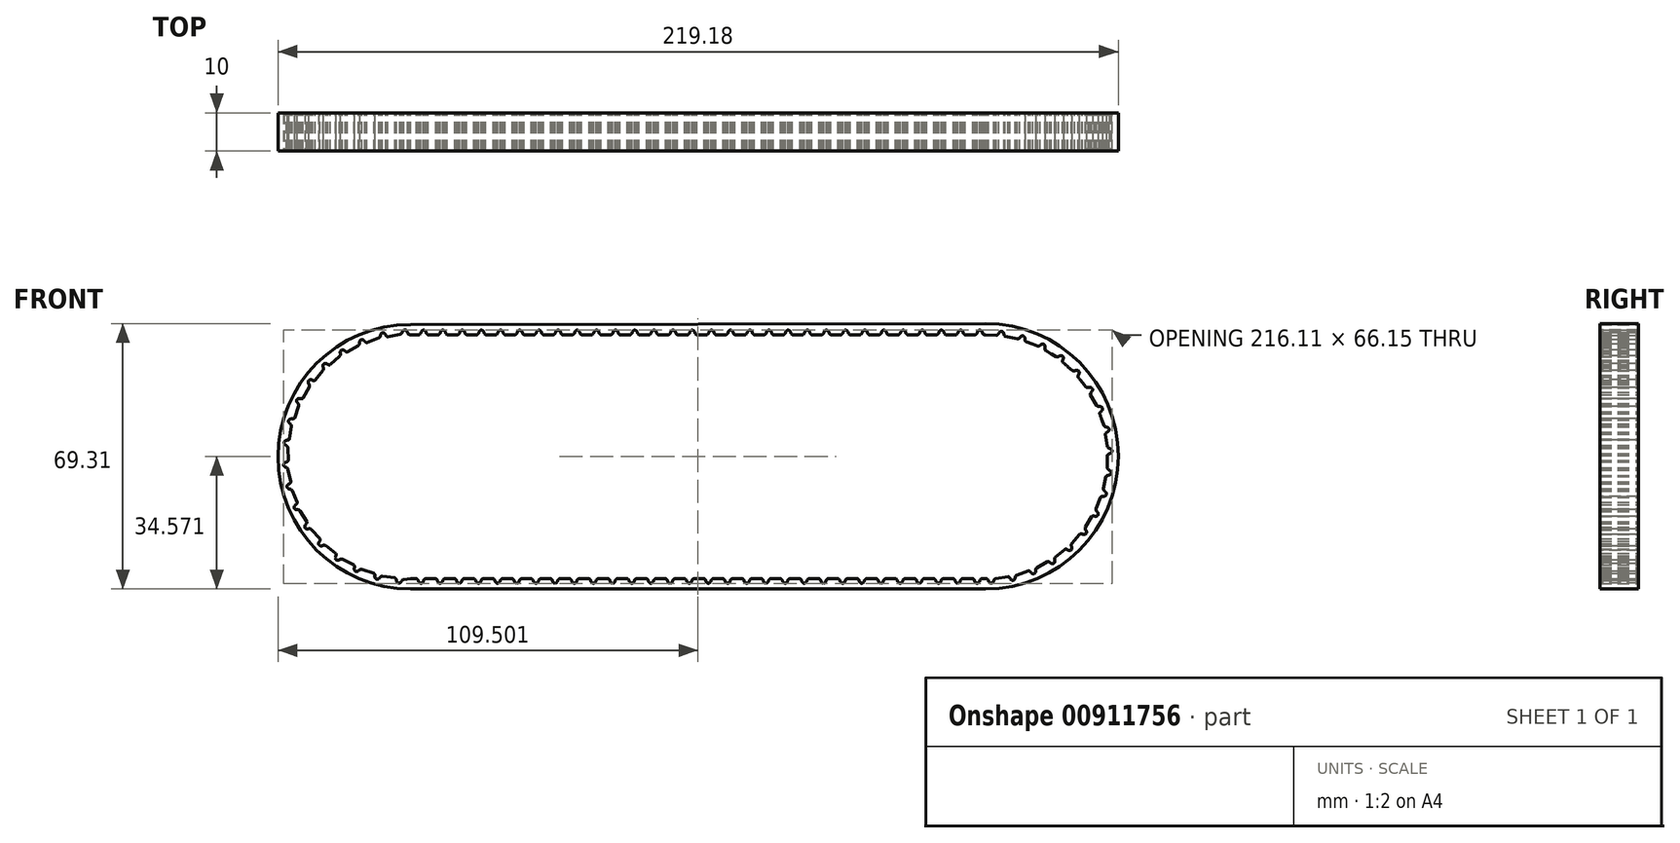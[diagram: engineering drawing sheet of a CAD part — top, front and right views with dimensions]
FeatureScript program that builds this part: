
annotation { "Feature Type Name" : "Feature", "Feature Type Description" : "" }
export const myFeature = defineFeature(function(context is Context, id is Id, definition is map)
    precondition{}
    {
        {
            var Q0;
            Q0=qCreatedBy(makeId("Front.planeOp"),FACE);
            var sketch = newSketch(context, id + "F0", { "sketchPlane" : qUnion([Q0])});
            skLineSegment(sketch, "E0", {"start": v(-83.51, -31.83) * mm, "end": v(-83.51, -31.83) * mm});
            skLineSegment(sketch, "E1", {"start": v(66.49, 31.83) * mm, "end": v(66.49, 31.83) * mm});
            skLineSegment(sketch, "E2", {"start": v(-83.51, 31.83) * mm, "end": v(-81.28, 31.83) * mm});
            skLineSegment(sketch, "E3", {"start": v(-83.51, -31.83) * mm, "end": v(-82.23, -31.83) * mm});
            skLineSegment(sketch, "E4", {"start": v(-83.51, -34.53) * mm, "end": v(-83.51, -34.53) * mm});
            skArc(sketch, "E5", {"start": v(66.49, 34.78) * mm, "mid": v(66.46, 34.78) * mm, "end": v(66.43, 34.78) * mm});
            skLineSegment(sketch, "E6", {"start": v(-83.51, -34.53) * mm, "end": v(66.49, -34.53) * mm});
            skArc(sketch, "E7", {"start": v(-83.51, 31.83) * mm, "mid": v(-83.53, 31.83) * mm, "end": v(-83.54, 31.83) * mm});
            skPoint(sketch, "E8", {"position": v(-75, 33.03) * mm});
            skEllipticalArc(sketch, "E9.1.0.0", {});
            skPoint(sketch, "E9.1.0.1", {"position": v(-70, 33.03) * mm});
            skArc(sketch, "E9.1.0.2", {"start": v(-69.27, 32.27) * mm, "mid": v(-69.1, 32) * mm, "end": v(-68.85, 31.83) * mm});
            skEllipticalArc(sketch, "E9.2.0.0", {});
            skPoint(sketch, "E9.2.0.1", {"position": v(-65, 33.03) * mm});
            skArc(sketch, "E9.2.0.2", {"start": v(-64.27, 32.27) * mm, "mid": v(-64.1, 32) * mm, "end": v(-63.85, 31.83) * mm});
            skEllipticalArc(sketch, "E9.3.0.0", {});
            skPoint(sketch, "E9.3.0.1", {"position": v(-60, 33.03) * mm});
            skArc(sketch, "E9.3.0.2", {"start": v(-59.27, 32.27) * mm, "mid": v(-59.1, 32) * mm, "end": v(-58.85, 31.83) * mm});
            skEllipticalArc(sketch, "E9.4.0.0", {});
            skPoint(sketch, "E9.4.0.1", {"position": v(-55, 33.03) * mm});
            skArc(sketch, "E9.4.0.2", {"start": v(-54.27, 32.27) * mm, "mid": v(-54.1, 32) * mm, "end": v(-53.85, 31.83) * mm});
            skEllipticalArc(sketch, "E9.5.0.0", {});
            skPoint(sketch, "E9.5.0.1", {"position": v(-50, 33.03) * mm});
            skArc(sketch, "E9.5.0.2", {"start": v(-49.27, 32.27) * mm, "mid": v(-49.1, 32) * mm, "end": v(-48.85, 31.83) * mm});
            skEllipticalArc(sketch, "E9.6.0.0", {});
            skPoint(sketch, "E9.6.0.1", {"position": v(-45, 33.03) * mm});
            skArc(sketch, "E9.6.0.2", {"start": v(-44.27, 32.27) * mm, "mid": v(-44.1, 32) * mm, "end": v(-43.85, 31.83) * mm});
            skEllipticalArc(sketch, "E9.7.0.0", {});
            skPoint(sketch, "E9.7.0.1", {"position": v(-40, 33.03) * mm});
            skArc(sketch, "E9.7.0.2", {"start": v(-39.27, 32.27) * mm, "mid": v(-39.1, 32) * mm, "end": v(-38.85, 31.83) * mm});
            skEllipticalArc(sketch, "E9.8.0.0", {});
            skPoint(sketch, "E9.8.0.1", {"position": v(-35, 33.03) * mm});
            skArc(sketch, "E9.8.0.2", {"start": v(-34.27, 32.27) * mm, "mid": v(-34.1, 32) * mm, "end": v(-33.85, 31.83) * mm});
            skEllipticalArc(sketch, "E9.9.0.0", {});
            skPoint(sketch, "E9.9.0.1", {"position": v(-30, 33.03) * mm});
            skArc(sketch, "E9.9.0.2", {"start": v(-29.27, 32.27) * mm, "mid": v(-29.1, 32) * mm, "end": v(-28.85, 31.83) * mm});
            skEllipticalArc(sketch, "E9.10.0.0", {});
            skPoint(sketch, "E9.10.0.1", {"position": v(-25, 33.03) * mm});
            skArc(sketch, "E9.10.0.2", {"start": v(-24.27, 32.27) * mm, "mid": v(-24.1, 32) * mm, "end": v(-23.85, 31.83) * mm});
            skEllipticalArc(sketch, "E9.11.0.0", {});
            skPoint(sketch, "E9.11.0.1", {"position": v(-20, 33.03) * mm});
            skArc(sketch, "E9.11.0.2", {"start": v(-19.27, 32.27) * mm, "mid": v(-19.1, 32) * mm, "end": v(-18.85, 31.83) * mm});
            skEllipticalArc(sketch, "E9.12.0.0", {});
            skPoint(sketch, "E9.12.0.1", {"position": v(-15, 33.03) * mm});
            skArc(sketch, "E9.12.0.2", {"start": v(-14.27, 32.27) * mm, "mid": v(-14.1, 32) * mm, "end": v(-13.85, 31.83) * mm});
            skEllipticalArc(sketch, "E9.13.0.0", {});
            skPoint(sketch, "E9.13.0.1", {"position": v(-10, 33.03) * mm});
            skArc(sketch, "E9.13.0.2", {"start": v(-9.27, 32.27) * mm, "mid": v(-9.1, 32) * mm, "end": v(-8.85, 31.83) * mm});
            skEllipticalArc(sketch, "E9.14.0.0", {});
            skPoint(sketch, "E9.14.0.1", {"position": v(-5, 33.03) * mm});
            skArc(sketch, "E9.14.0.2", {"start": v(-4.27, 32.27) * mm, "mid": v(-4.1, 32) * mm, "end": v(-3.85, 31.83) * mm});
            skEllipticalArc(sketch, "E9.15.0.0", {});
            skPoint(sketch, "E9.15.0.1", {"position": v(0, 33.03) * mm});
            skArc(sketch, "E9.15.0.2", {"start": v(0.73, 32.27) * mm, "mid": v(0.9, 32) * mm, "end": v(1.15, 31.83) * mm});
            skEllipticalArc(sketch, "E9.16.0.0", {});
            skPoint(sketch, "E9.16.0.1", {"position": v(5, 33.03) * mm});
            skArc(sketch, "E9.16.0.2", {"start": v(5.73, 32.27) * mm, "mid": v(5.9, 32) * mm, "end": v(6.15, 31.83) * mm});
            skEllipticalArc(sketch, "E9.17.0.0", {});
            skPoint(sketch, "E9.17.0.1", {"position": v(10, 33.03) * mm});
            skArc(sketch, "E9.17.0.2", {"start": v(10.73, 32.27) * mm, "mid": v(10.9, 32) * mm, "end": v(11.15, 31.83) * mm});
            skEllipticalArc(sketch, "E9.18.0.0", {});
            skPoint(sketch, "E9.18.0.1", {"position": v(15, 33.03) * mm});
            skArc(sketch, "E9.18.0.2", {"start": v(15.73, 32.27) * mm, "mid": v(15.9, 32) * mm, "end": v(16.15, 31.83) * mm});
            skEllipticalArc(sketch, "E9.19.0.0", {});
            skPoint(sketch, "E9.19.0.1", {"position": v(20, 33.03) * mm});
            skArc(sketch, "E9.19.0.2", {"start": v(20.73, 32.27) * mm, "mid": v(20.9, 32) * mm, "end": v(21.15, 31.83) * mm});
            skEllipticalArc(sketch, "E9.20.0.0", {});
            skPoint(sketch, "E9.20.0.1", {"position": v(25, 33.03) * mm});
            skArc(sketch, "E9.20.0.2", {"start": v(25.73, 32.27) * mm, "mid": v(25.9, 32) * mm, "end": v(26.15, 31.83) * mm});
            skEllipticalArc(sketch, "E9.21.0.0", {});
            skPoint(sketch, "E9.21.0.1", {"position": v(30, 33.03) * mm});
            skArc(sketch, "E9.21.0.2", {"start": v(30.73, 32.27) * mm, "mid": v(30.9, 32) * mm, "end": v(31.15, 31.83) * mm});
            skEllipticalArc(sketch, "E9.22.0.0", {});
            skPoint(sketch, "E9.22.0.1", {"position": v(35, 33.03) * mm});
            skArc(sketch, "E9.22.0.2", {"start": v(35.73, 32.27) * mm, "mid": v(35.9, 32) * mm, "end": v(36.15, 31.83) * mm});
            skEllipticalArc(sketch, "E9.23.0.0", {});
            skPoint(sketch, "E9.23.0.1", {"position": v(40, 33.03) * mm});
            skArc(sketch, "E9.23.0.2", {"start": v(40.73, 32.27) * mm, "mid": v(40.9, 32) * mm, "end": v(41.15, 31.83) * mm});
            skEllipticalArc(sketch, "E9.24.0.0", {});
            skPoint(sketch, "E9.24.0.1", {"position": v(45, 33.03) * mm});
            skArc(sketch, "E9.24.0.2", {"start": v(45.73, 32.27) * mm, "mid": v(45.9, 32) * mm, "end": v(46.15, 31.83) * mm});
            skEllipticalArc(sketch, "E9.25.0.0", {});
            skPoint(sketch, "E9.25.0.1", {"position": v(50, 33.03) * mm});
            skArc(sketch, "E9.25.0.2", {"start": v(50.73, 32.27) * mm, "mid": v(50.9, 32) * mm, "end": v(51.15, 31.83) * mm});
            skEllipticalArc(sketch, "E9.26.0.0", {});
            skPoint(sketch, "E9.26.0.1", {"position": v(55, 33.03) * mm});
            skArc(sketch, "E9.26.0.2", {"start": v(55.73, 32.27) * mm, "mid": v(55.9, 32) * mm, "end": v(56.15, 31.83) * mm});
            skEllipticalArc(sketch, "E9.27.0.0", {});
            skPoint(sketch, "E9.27.0.1", {"position": v(60, 33.03) * mm});
            skArc(sketch, "E9.27.0.2", {"start": v(60.73, 32.27) * mm, "mid": v(60.9, 32) * mm, "end": v(61.15, 31.83) * mm});
            skEllipticalArc(sketch, "E9.28.0.0", {});
            skPoint(sketch, "E9.28.0.1", {"position": v(65, 33.03) * mm});
            skArc(sketch, "E9.28.0.2", {"start": v(65.73, 32.27) * mm, "mid": v(65.9, 32) * mm, "end": v(66.15, 31.83) * mm});
            skLineSegment(sketch, "E9.direction1", {"start": v(-75, 32.03) * mm, "end": v(-70, 32.03) * mm, "construction": true});
            skEllipticalArc(sketch, "E10", {});
            skArc(sketch, "E11", {"start": v(-71.2, 31.83) * mm, "mid": v(-70.9, 32) * mm, "end": v(-70.7, 32.27) * mm});
            skEllipticalArc(sketch, "E12.1.0.0", {});
            skArc(sketch, "E12.1.0.1", {"start": v(-66.2, 31.83) * mm, "mid": v(-65.9, 32) * mm, "end": v(-65.7, 32.27) * mm});
            skEllipticalArc(sketch, "E12.2.0.0", {});
            skArc(sketch, "E12.2.0.1", {"start": v(-61.2, 31.83) * mm, "mid": v(-60.9, 32) * mm, "end": v(-60.7, 32.27) * mm});
            skEllipticalArc(sketch, "E13.0.3.0", {});
            skArc(sketch, "E13.4.3.0", {"start": v(-56.2, 31.83) * mm, "mid": v(-55.9, 32) * mm, "end": v(-55.7, 32.27) * mm});
            skEllipticalArc(sketch, "E13.0.4.0", {});
            skArc(sketch, "E13.4.4.0", {"start": v(-51.2, 31.83) * mm, "mid": v(-50.9, 32) * mm, "end": v(-50.7, 32.27) * mm});
            skEllipticalArc(sketch, "E13.0.5.0", {});
            skArc(sketch, "E13.4.5.0", {"start": v(-46.2, 31.83) * mm, "mid": v(-45.9, 32) * mm, "end": v(-45.7, 32.27) * mm});
            skEllipticalArc(sketch, "E13.0.6.0", {});
            skArc(sketch, "E13.4.6.0", {"start": v(-41.2, 31.83) * mm, "mid": v(-40.9, 32) * mm, "end": v(-40.7, 32.27) * mm});
            skEllipticalArc(sketch, "E13.0.7.0", {});
            skArc(sketch, "E13.4.7.0", {"start": v(-36.2, 31.83) * mm, "mid": v(-35.9, 32) * mm, "end": v(-35.7, 32.27) * mm});
            skEllipticalArc(sketch, "E13.0.8.0", {});
            skArc(sketch, "E13.4.8.0", {"start": v(-31.2, 31.83) * mm, "mid": v(-30.9, 32) * mm, "end": v(-30.7, 32.27) * mm});
            skEllipticalArc(sketch, "E13.0.9.0", {});
            skArc(sketch, "E13.4.9.0", {"start": v(-26.2, 31.83) * mm, "mid": v(-25.9, 32) * mm, "end": v(-25.7, 32.27) * mm});
            skEllipticalArc(sketch, "E13.0.10.0", {});
            skArc(sketch, "E13.4.10.0", {"start": v(-21.2, 31.83) * mm, "mid": v(-20.9, 32) * mm, "end": v(-20.7, 32.27) * mm});
            skEllipticalArc(sketch, "E13.0.11.0", {});
            skArc(sketch, "E13.4.11.0", {"start": v(-16.2, 31.83) * mm, "mid": v(-15.9, 32) * mm, "end": v(-15.7, 32.27) * mm});
            skEllipticalArc(sketch, "E13.0.12.0", {});
            skArc(sketch, "E13.4.12.0", {"start": v(-11.2, 31.83) * mm, "mid": v(-10.9, 32) * mm, "end": v(-10.7, 32.27) * mm});
            skEllipticalArc(sketch, "E13.0.13.0", {});
            skArc(sketch, "E13.4.13.0", {"start": v(-6.2, 31.83) * mm, "mid": v(-5.9, 32) * mm, "end": v(-5.7, 32.27) * mm});
            skEllipticalArc(sketch, "E13.0.14.0", {});
            skArc(sketch, "E13.4.14.0", {"start": v(-1.2, 31.83) * mm, "mid": v(-0.9, 32) * mm, "end": v(-0.7, 32.27) * mm});
            skEllipticalArc(sketch, "E13.0.15.0", {});
            skArc(sketch, "E13.4.15.0", {"start": v(3.8, 31.83) * mm, "mid": v(4.1, 32) * mm, "end": v(4.3, 32.27) * mm});
            skEllipticalArc(sketch, "E13.0.16.0", {});
            skArc(sketch, "E13.4.16.0", {"start": v(8.8, 31.83) * mm, "mid": v(9.1, 32) * mm, "end": v(9.3, 32.27) * mm});
            skEllipticalArc(sketch, "E13.0.17.0", {});
            skArc(sketch, "E13.4.17.0", {"start": v(13.8, 31.83) * mm, "mid": v(14.1, 32) * mm, "end": v(14.3, 32.27) * mm});
            skEllipticalArc(sketch, "E13.0.18.0", {});
            skArc(sketch, "E13.4.18.0", {"start": v(18.8, 31.83) * mm, "mid": v(19.1, 32) * mm, "end": v(19.3, 32.27) * mm});
            skEllipticalArc(sketch, "E13.0.19.0", {});
            skArc(sketch, "E13.4.19.0", {"start": v(23.8, 31.83) * mm, "mid": v(24.1, 32) * mm, "end": v(24.3, 32.27) * mm});
            skEllipticalArc(sketch, "E13.0.20.0", {});
            skArc(sketch, "E13.4.20.0", {"start": v(28.8, 31.83) * mm, "mid": v(29.1, 32) * mm, "end": v(29.3, 32.27) * mm});
            skEllipticalArc(sketch, "E13.0.21.0", {});
            skArc(sketch, "E13.4.21.0", {"start": v(33.8, 31.83) * mm, "mid": v(34.1, 32) * mm, "end": v(34.3, 32.27) * mm});
            skEllipticalArc(sketch, "E13.0.22.0", {});
            skArc(sketch, "E13.4.22.0", {"start": v(38.8, 31.83) * mm, "mid": v(39.1, 32) * mm, "end": v(39.3, 32.27) * mm});
            skEllipticalArc(sketch, "E13.0.23.0", {});
            skArc(sketch, "E13.4.23.0", {"start": v(43.8, 31.83) * mm, "mid": v(44.1, 32) * mm, "end": v(44.3, 32.27) * mm});
            skEllipticalArc(sketch, "E13.0.24.0", {});
            skArc(sketch, "E13.4.24.0", {"start": v(48.8, 31.83) * mm, "mid": v(49.1, 32) * mm, "end": v(49.3, 32.27) * mm});
            skEllipticalArc(sketch, "E13.0.25.0", {});
            skArc(sketch, "E13.4.25.0", {"start": v(53.8, 31.83) * mm, "mid": v(54.1, 32) * mm, "end": v(54.3, 32.27) * mm});
            skEllipticalArc(sketch, "E13.0.26.0", {});
            skArc(sketch, "E13.4.26.0", {"start": v(58.8, 31.83) * mm, "mid": v(59.1, 32) * mm, "end": v(59.3, 32.27) * mm});
            skEllipticalArc(sketch, "E13.0.27.0", {});
            skArc(sketch, "E13.4.27.0", {"start": v(63.8, 31.83) * mm, "mid": v(64.1, 32) * mm, "end": v(64.3, 32.27) * mm});
            skEllipticalArc(sketch, "E14.1.0.0", {});
            skArc(sketch, "E14.1.0.1", {"start": v(-76.24, 31.83) * mm, "mid": v(-75.94, 32) * mm, "end": v(-75.74, 32.27) * mm});
            skEllipticalArc(sketch, "E14.2.0.0", {});
            skArc(sketch, "E14.2.0.1", {"start": v(-81.28, 31.83) * mm, "mid": v(-80.98, 32) * mm, "end": v(-80.79, 32.27) * mm});
            skEllipticalArc(sketch, "E15.1.0.0", {});
            skArc(sketch, "E15.1.0.1", {"start": v(-74.32, 32.27) * mm, "mid": v(-74.16, 32) * mm, "end": v(-73.9, 31.83) * mm});
            skEllipticalArc(sketch, "E15.2.0.0", {});
            skArc(sketch, "E15.2.0.1", {"start": v(-79.37, 32.27) * mm, "mid": v(-79.2, 32) * mm, "end": v(-78.95, 31.83) * mm});
            skLineSegment(sketch, "E15.direction1", {"start": v(-70, 32.03) * mm, "end": v(-75.05, 32.03) * mm, "construction": true});
            skPoint(sketch, "E16", {"position": v(59.24, -33.03) * mm});
            skEllipticalArc(sketch, "E17.1.0.0", {});
            skPoint(sketch, "E17.1.0.1", {"position": v(54.24, -33.03) * mm});
            skArc(sketch, "E17.1.0.2", {"start": v(53.5, -32.28) * mm, "mid": v(53.34, -32) * mm, "end": v(53.08, -31.83) * mm});
            skEllipticalArc(sketch, "E17.2.0.0", {});
            skPoint(sketch, "E17.2.0.1", {"position": v(49.24, -33.03) * mm});
            skArc(sketch, "E17.2.0.2", {"start": v(48.5, -32.28) * mm, "mid": v(48.34, -32) * mm, "end": v(48.08, -31.83) * mm});
            skEllipticalArc(sketch, "E17.3.0.0", {});
            skPoint(sketch, "E17.3.0.1", {"position": v(44.24, -33.03) * mm});
            skArc(sketch, "E17.3.0.2", {"start": v(43.5, -32.28) * mm, "mid": v(43.34, -32) * mm, "end": v(43.08, -31.83) * mm});
            skEllipticalArc(sketch, "E17.4.0.0", {});
            skPoint(sketch, "E17.4.0.1", {"position": v(39.24, -33.03) * mm});
            skArc(sketch, "E17.4.0.2", {"start": v(38.5, -32.28) * mm, "mid": v(38.34, -32) * mm, "end": v(38.08, -31.83) * mm});
            skEllipticalArc(sketch, "E17.5.0.0", {});
            skPoint(sketch, "E17.5.0.1", {"position": v(34.24, -33.03) * mm});
            skArc(sketch, "E17.5.0.2", {"start": v(33.5, -32.28) * mm, "mid": v(33.34, -32) * mm, "end": v(33.08, -31.83) * mm});
            skEllipticalArc(sketch, "E17.6.0.0", {});
            skPoint(sketch, "E17.6.0.1", {"position": v(29.24, -33.03) * mm});
            skArc(sketch, "E17.6.0.2", {"start": v(28.5, -32.28) * mm, "mid": v(28.34, -32) * mm, "end": v(28.08, -31.83) * mm});
            skEllipticalArc(sketch, "E17.7.0.0", {});
            skPoint(sketch, "E17.7.0.1", {"position": v(24.24, -33.03) * mm});
            skArc(sketch, "E17.7.0.2", {"start": v(23.5, -32.28) * mm, "mid": v(23.34, -32) * mm, "end": v(23.08, -31.83) * mm});
            skEllipticalArc(sketch, "E17.8.0.0", {});
            skPoint(sketch, "E17.8.0.1", {"position": v(19.24, -33.03) * mm});
            skArc(sketch, "E17.8.0.2", {"start": v(18.5, -32.28) * mm, "mid": v(18.34, -32) * mm, "end": v(18.08, -31.83) * mm});
            skEllipticalArc(sketch, "E17.9.0.0", {});
            skPoint(sketch, "E17.9.0.1", {"position": v(14.24, -33.03) * mm});
            skArc(sketch, "E17.9.0.2", {"start": v(13.5, -32.28) * mm, "mid": v(13.34, -32) * mm, "end": v(13.08, -31.83) * mm});
            skEllipticalArc(sketch, "E17.10.0.0", {});
            skPoint(sketch, "E17.10.0.1", {"position": v(9.24, -33.03) * mm});
            skArc(sketch, "E17.10.0.2", {"start": v(8.5, -32.28) * mm, "mid": v(8.34, -32) * mm, "end": v(8.08, -31.83) * mm});
            skEllipticalArc(sketch, "E17.11.0.0", {});
            skPoint(sketch, "E17.11.0.1", {"position": v(4.24, -33.03) * mm});
            skArc(sketch, "E17.11.0.2", {"start": v(3.5, -32.28) * mm, "mid": v(3.34, -32) * mm, "end": v(3.08, -31.83) * mm});
            skEllipticalArc(sketch, "E17.12.0.0", {});
            skPoint(sketch, "E17.12.0.1", {"position": v(-0.76, -33.03) * mm});
            skArc(sketch, "E17.12.0.2", {"start": v(-1.5, -32.28) * mm, "mid": v(-1.66, -32) * mm, "end": v(-1.92, -31.83) * mm});
            skEllipticalArc(sketch, "E17.13.0.0", {});
            skPoint(sketch, "E17.13.0.1", {"position": v(-5.76, -33.03) * mm});
            skArc(sketch, "E17.13.0.2", {"start": v(-6.5, -32.28) * mm, "mid": v(-6.66, -32) * mm, "end": v(-6.92, -31.83) * mm});
            skEllipticalArc(sketch, "E17.14.0.0", {});
            skPoint(sketch, "E17.14.0.1", {"position": v(-10.76, -33.03) * mm});
            skArc(sketch, "E17.14.0.2", {"start": v(-11.5, -32.28) * mm, "mid": v(-11.66, -32) * mm, "end": v(-11.92, -31.83) * mm});
            skEllipticalArc(sketch, "E17.15.0.0", {});
            skPoint(sketch, "E17.15.0.1", {"position": v(-15.76, -33.03) * mm});
            skArc(sketch, "E17.15.0.2", {"start": v(-16.5, -32.28) * mm, "mid": v(-16.66, -32) * mm, "end": v(-16.92, -31.83) * mm});
            skEllipticalArc(sketch, "E17.16.0.0", {});
            skPoint(sketch, "E17.16.0.1", {"position": v(-20.76, -33.03) * mm});
            skArc(sketch, "E17.16.0.2", {"start": v(-21.5, -32.28) * mm, "mid": v(-21.66, -32) * mm, "end": v(-21.92, -31.83) * mm});
            skEllipticalArc(sketch, "E17.17.0.0", {});
            skPoint(sketch, "E17.17.0.1", {"position": v(-25.76, -33.03) * mm});
            skArc(sketch, "E17.17.0.2", {"start": v(-26.5, -32.28) * mm, "mid": v(-26.66, -32) * mm, "end": v(-26.92, -31.83) * mm});
            skEllipticalArc(sketch, "E17.18.0.0", {});
            skPoint(sketch, "E17.18.0.1", {"position": v(-30.76, -33.03) * mm});
            skArc(sketch, "E17.18.0.2", {"start": v(-31.5, -32.28) * mm, "mid": v(-31.66, -32) * mm, "end": v(-31.92, -31.83) * mm});
            skEllipticalArc(sketch, "E17.19.0.0", {});
            skPoint(sketch, "E17.19.0.1", {"position": v(-35.76, -33.03) * mm});
            skArc(sketch, "E17.19.0.2", {"start": v(-36.5, -32.28) * mm, "mid": v(-36.66, -32) * mm, "end": v(-36.92, -31.83) * mm});
            skEllipticalArc(sketch, "E17.20.0.0", {});
            skPoint(sketch, "E17.20.0.1", {"position": v(-40.76, -33.03) * mm});
            skArc(sketch, "E17.20.0.2", {"start": v(-41.5, -32.28) * mm, "mid": v(-41.66, -32) * mm, "end": v(-41.92, -31.83) * mm});
            skEllipticalArc(sketch, "E17.21.0.0", {});
            skPoint(sketch, "E17.21.0.1", {"position": v(-45.76, -33.03) * mm});
            skArc(sketch, "E17.21.0.2", {"start": v(-46.5, -32.28) * mm, "mid": v(-46.66, -32) * mm, "end": v(-46.92, -31.83) * mm});
            skEllipticalArc(sketch, "E17.22.0.0", {});
            skPoint(sketch, "E17.22.0.1", {"position": v(-50.76, -33.03) * mm});
            skArc(sketch, "E17.22.0.2", {"start": v(-51.5, -32.28) * mm, "mid": v(-51.66, -32) * mm, "end": v(-51.92, -31.83) * mm});
            skEllipticalArc(sketch, "E17.23.0.0", {});
            skPoint(sketch, "E17.23.0.1", {"position": v(-55.76, -33.03) * mm});
            skArc(sketch, "E17.23.0.2", {"start": v(-56.5, -32.28) * mm, "mid": v(-56.66, -32) * mm, "end": v(-56.92, -31.83) * mm});
            skEllipticalArc(sketch, "E17.24.0.0", {});
            skPoint(sketch, "E17.24.0.1", {"position": v(-60.76, -33.03) * mm});
            skArc(sketch, "E17.24.0.2", {"start": v(-61.5, -32.28) * mm, "mid": v(-61.66, -32) * mm, "end": v(-61.92, -31.83) * mm});
            skEllipticalArc(sketch, "E17.25.0.0", {});
            skPoint(sketch, "E17.25.0.1", {"position": v(-65.76, -33.03) * mm});
            skArc(sketch, "E17.25.0.2", {"start": v(-66.5, -32.28) * mm, "mid": v(-66.66, -32) * mm, "end": v(-66.92, -31.83) * mm});
            skEllipticalArc(sketch, "E17.26.0.0", {});
            skPoint(sketch, "E17.26.0.1", {"position": v(-70.76, -33.03) * mm});
            skArc(sketch, "E17.26.0.2", {"start": v(-71.5, -32.28) * mm, "mid": v(-71.66, -32) * mm, "end": v(-71.92, -31.83) * mm});
            skEllipticalArc(sketch, "E17.27.0.0", {});
            skPoint(sketch, "E17.27.0.1", {"position": v(-75.76, -33.03) * mm});
            skArc(sketch, "E17.27.0.2", {"start": v(-76.5, -32.28) * mm, "mid": v(-76.66, -32) * mm, "end": v(-76.92, -31.83) * mm});
            skEllipticalArc(sketch, "E17.28.0.0", {});
            skPoint(sketch, "E17.28.0.1", {"position": v(-80.76, -33.03) * mm});
            skArc(sketch, "E17.28.0.2", {"start": v(-81.5, -32.28) * mm, "mid": v(-81.66, -32) * mm, "end": v(-81.92, -31.83) * mm});
            skEllipticalArc(sketch, "E18", {});
            skArc(sketch, "E19", {"start": v(55.43, -31.83) * mm, "mid": v(55.13, -32) * mm, "end": v(54.93, -32.28) * mm});
            skEllipticalArc(sketch, "E20.1.0.0", {});
            skArc(sketch, "E20.1.0.1", {"start": v(50.43, -31.83) * mm, "mid": v(50.13, -32) * mm, "end": v(49.93, -32.28) * mm});
            skEllipticalArc(sketch, "E20.2.0.0", {});
            skArc(sketch, "E20.2.0.1", {"start": v(45.43, -31.83) * mm, "mid": v(45.13, -32) * mm, "end": v(44.93, -32.28) * mm});
            skLineSegment(sketch, "E20.direction1", {"start": v(53.08, -31.83) * mm, "end": v(50.43, -31.83) * mm, "construction": true});
            skEllipticalArc(sketch, "E21.0.3.0", {});
            skArc(sketch, "E21.4.3.0", {"start": v(40.43, -31.83) * mm, "mid": v(40.13, -32) * mm, "end": v(39.93, -32.28) * mm});
            skEllipticalArc(sketch, "E21.0.4.0", {});
            skArc(sketch, "E21.4.4.0", {"start": v(35.43, -31.83) * mm, "mid": v(35.13, -32) * mm, "end": v(34.93, -32.28) * mm});
            skEllipticalArc(sketch, "E21.0.5.0", {});
            skArc(sketch, "E21.4.5.0", {"start": v(30.43, -31.83) * mm, "mid": v(30.13, -32) * mm, "end": v(29.93, -32.28) * mm});
            skEllipticalArc(sketch, "E21.0.6.0", {});
            skArc(sketch, "E21.4.6.0", {"start": v(25.43, -31.83) * mm, "mid": v(25.13, -32) * mm, "end": v(24.93, -32.28) * mm});
            skEllipticalArc(sketch, "E21.0.7.0", {});
            skArc(sketch, "E21.4.7.0", {"start": v(20.43, -31.83) * mm, "mid": v(20.13, -32) * mm, "end": v(19.93, -32.28) * mm});
            skEllipticalArc(sketch, "E21.0.8.0", {});
            skArc(sketch, "E21.4.8.0", {"start": v(15.43, -31.83) * mm, "mid": v(15.13, -32) * mm, "end": v(14.93, -32.28) * mm});
            skEllipticalArc(sketch, "E21.0.9.0", {});
            skArc(sketch, "E21.4.9.0", {"start": v(10.43, -31.83) * mm, "mid": v(10.13, -32) * mm, "end": v(9.93, -32.28) * mm});
            skEllipticalArc(sketch, "E21.0.10.0", {});
            skArc(sketch, "E21.4.10.0", {"start": v(5.43, -31.83) * mm, "mid": v(5.13, -32) * mm, "end": v(4.93, -32.28) * mm});
            skEllipticalArc(sketch, "E21.0.11.0", {});
            skArc(sketch, "E21.4.11.0", {"start": v(0.43, -31.83) * mm, "mid": v(0.13, -32) * mm, "end": v(-0.07, -32.28) * mm});
            skEllipticalArc(sketch, "E21.0.12.0", {});
            skArc(sketch, "E21.4.12.0", {"start": v(-4.57, -31.83) * mm, "mid": v(-4.87, -32) * mm, "end": v(-5.07, -32.28) * mm});
            skEllipticalArc(sketch, "E21.0.13.0", {});
            skArc(sketch, "E21.4.13.0", {"start": v(-9.57, -31.83) * mm, "mid": v(-9.87, -32) * mm, "end": v(-10.07, -32.28) * mm});
            skEllipticalArc(sketch, "E21.0.14.0", {});
            skArc(sketch, "E21.4.14.0", {"start": v(-14.57, -31.83) * mm, "mid": v(-14.87, -32) * mm, "end": v(-15.07, -32.28) * mm});
            skEllipticalArc(sketch, "E21.0.15.0", {});
            skArc(sketch, "E21.4.15.0", {"start": v(-19.57, -31.83) * mm, "mid": v(-19.87, -32) * mm, "end": v(-20.07, -32.28) * mm});
            skEllipticalArc(sketch, "E21.0.16.0", {});
            skArc(sketch, "E21.4.16.0", {"start": v(-24.57, -31.83) * mm, "mid": v(-24.87, -32) * mm, "end": v(-25.07, -32.28) * mm});
            skEllipticalArc(sketch, "E21.0.17.0", {});
            skArc(sketch, "E21.4.17.0", {"start": v(-29.57, -31.83) * mm, "mid": v(-29.87, -32) * mm, "end": v(-30.07, -32.28) * mm});
            skEllipticalArc(sketch, "E21.0.18.0", {});
            skArc(sketch, "E21.4.18.0", {"start": v(-34.57, -31.83) * mm, "mid": v(-34.87, -32) * mm, "end": v(-35.07, -32.28) * mm});
            skEllipticalArc(sketch, "E21.0.19.0", {});
            skArc(sketch, "E21.4.19.0", {"start": v(-39.57, -31.83) * mm, "mid": v(-39.87, -32) * mm, "end": v(-40.07, -32.28) * mm});
            skEllipticalArc(sketch, "E21.0.20.0", {});
            skArc(sketch, "E21.4.20.0", {"start": v(-44.57, -31.83) * mm, "mid": v(-44.87, -32) * mm, "end": v(-45.07, -32.28) * mm});
            skEllipticalArc(sketch, "E21.0.21.0", {});
            skArc(sketch, "E21.4.21.0", {"start": v(-49.57, -31.83) * mm, "mid": v(-49.87, -32) * mm, "end": v(-50.07, -32.28) * mm});
            skEllipticalArc(sketch, "E21.0.22.0", {});
            skArc(sketch, "E21.4.22.0", {"start": v(-54.57, -31.83) * mm, "mid": v(-54.87, -32) * mm, "end": v(-55.07, -32.28) * mm});
            skEllipticalArc(sketch, "E21.0.23.0", {});
            skArc(sketch, "E21.4.23.0", {"start": v(-59.57, -31.83) * mm, "mid": v(-59.87, -32) * mm, "end": v(-60.07, -32.28) * mm});
            skEllipticalArc(sketch, "E21.0.24.0", {});
            skArc(sketch, "E21.4.24.0", {"start": v(-64.57, -31.83) * mm, "mid": v(-64.87, -32) * mm, "end": v(-65.07, -32.28) * mm});
            skEllipticalArc(sketch, "E21.0.25.0", {});
            skArc(sketch, "E21.4.25.0", {"start": v(-69.57, -31.83) * mm, "mid": v(-69.87, -32) * mm, "end": v(-70.07, -32.28) * mm});
            skEllipticalArc(sketch, "E21.0.26.0", {});
            skArc(sketch, "E21.4.26.0", {"start": v(-74.57, -31.83) * mm, "mid": v(-74.87, -32) * mm, "end": v(-75.07, -32.28) * mm});
            skEllipticalArc(sketch, "E21.0.27.0", {});
            skArc(sketch, "E21.4.27.0", {"start": v(-79.57, -31.83) * mm, "mid": v(-79.87, -32) * mm, "end": v(-80.07, -32.28) * mm});
            skEllipticalArc(sketch, "E22.1.0.0", {});
            skArc(sketch, "E22.1.0.1", {"start": v(60.48, -31.83) * mm, "mid": v(60.17, -32) * mm, "end": v(59.98, -32.28) * mm});
            skEllipticalArc(sketch, "E22.2.0.0", {});
            skArc(sketch, "E22.2.0.1", {"start": v(65.52, -31.83) * mm, "mid": v(65.22, -32) * mm, "end": v(65.02, -32.28) * mm});
            skLineSegment(sketch, "E22.direction1", {"start": v(55.43, -31.83) * mm, "end": v(58.13, -31.83) * mm, "construction": true});
            skEllipticalArc(sketch, "E23.1.0.0", {});
            skArc(sketch, "E23.1.0.1", {"start": v(58.56, -32.28) * mm, "mid": v(58.4, -32) * mm, "end": v(58.13, -31.83) * mm});
            skEllipticalArc(sketch, "E23.2.0.0", {});
            skArc(sketch, "E23.2.0.1", {"start": v(63.6, -32.28) * mm, "mid": v(63.44, -32) * mm, "end": v(63.18, -31.83) * mm});
            skEllipticalArc(sketch, "E24.1.0", {});
            skEllipticalArc(sketch, "E24.1.1", {});
            skArc(sketch, "E24.1.2", {"start": v(69.35, 31.7) * mm, "mid": v(69.67, 31.82) * mm, "end": v(69.9, 32.07) * mm});
            skArc(sketch, "E24.1.3", {"start": v(71.32, 31.9) * mm, "mid": v(71.42, 31.63) * mm, "end": v(71.62, 31.44) * mm});
            skPoint(sketch, "E24.1.4", {"position": v(70.7, 32.73) * mm});
            skEllipticalArc(sketch, "E24.2.0", {});
            skEllipticalArc(sketch, "E24.2.1", {});
            skArc(sketch, "E24.2.2", {"start": v(74.82, 30.76) * mm, "mid": v(75.15, 30.82) * mm, "end": v(75.43, 31.02) * mm});
            skArc(sketch, "E24.2.3", {"start": v(76.78, 30.57) * mm, "mid": v(76.84, 30.3) * mm, "end": v(77, 30.07) * mm});
            skPoint(sketch, "E24.2.4", {"position": v(76.3, 31.51) * mm});
            skEllipticalArc(sketch, "E24.3.0", {});
            skEllipticalArc(sketch, "E24.3.1", {});
            skArc(sketch, "E24.3.2", {"start": v(80.08, 28.9) * mm, "mid": v(80.42, 28.9) * mm, "end": v(80.73, 29.04) * mm});
            skArc(sketch, "E24.3.3", {"start": v(81.97, 28.33) * mm, "mid": v(81.97, 28.04) * mm, "end": v(82.08, 27.77) * mm});
            skPoint(sketch, "E24.3.4", {"position": v(81.71, 29.35) * mm});
            skEllipticalArc(sketch, "E24.4.0", {});
            skEllipticalArc(sketch, "E24.4.1", {});
            skArc(sketch, "E24.4.2", {"start": v(84.9, 26.1) * mm, "mid": v(85.23, 26.04) * mm, "end": v(85.56, 26.13) * mm});
            skArc(sketch, "E24.4.3", {"start": v(86.65, 25.21) * mm, "mid": v(86.6, 24.92) * mm, "end": v(86.67, 24.64) * mm});
            skPoint(sketch, "E24.4.4", {"position": v(86.58, 26.26) * mm});
            skEllipticalArc(sketch, "E24.5.0", {});
            skEllipticalArc(sketch, "E24.5.1", {});
            skArc(sketch, "E24.5.2", {"start": v(89.15, 22.51) * mm, "mid": v(89.46, 22.39) * mm, "end": v(89.8, 22.42) * mm});
            skArc(sketch, "E24.5.3", {"start": v(90.72, 21.33) * mm, "mid": v(90.63, 21.05) * mm, "end": v(90.64, 20.76) * mm});
            skPoint(sketch, "E24.5.4", {"position": v(90.83, 22.37) * mm});
            skEllipticalArc(sketch, "E24.6.0", {});
            skEllipticalArc(sketch, "E24.6.1", {});
            skArc(sketch, "E24.6.2", {"start": v(92.71, 18.24) * mm, "mid": v(93, 18.06) * mm, "end": v(93.34, 18.03) * mm});
            skArc(sketch, "E24.6.3", {"start": v(94.06, 16.8) * mm, "mid": v(93.9, 16.52) * mm, "end": v(93.89, 16.2) * mm});
            skPoint(sketch, "E24.6.4", {"position": v(94.35, 17.8) * mm});
            skEllipticalArc(sketch, "E24.7.0", {});
            skEllipticalArc(sketch, "E24.7.1", {});
            skArc(sketch, "E24.7.2", {"start": v(95.48, 13.4) * mm, "mid": v(95.74, 13.18) * mm, "end": v(96.07, 13.1) * mm});
            skArc(sketch, "E24.7.3", {"start": v(96.55, 11.75) * mm, "mid": v(96.37, 11.53) * mm, "end": v(96.29, 11.25) * mm});
            skPoint(sketch, "E24.7.4", {"position": v(97.02, 12.7) * mm});
            skEllipticalArc(sketch, "E24.8.0", {});
            skEllipticalArc(sketch, "E24.8.1", {});
            skArc(sketch, "E24.8.2", {"start": v(97.37, 8.17) * mm, "mid": v(97.58, 7.9) * mm, "end": v(97.9, 7.76) * mm});
            skArc(sketch, "E24.8.3", {"start": v(98.14, 6.35) * mm, "mid": v(97.9, 6.14) * mm, "end": v(97.77, 5.85) * mm});
            skPoint(sketch, "E24.8.4", {"position": v(98.76, 7.2) * mm});
            skEllipticalArc(sketch, "E24.9.0", {});
            skEllipticalArc(sketch, "E24.9.1", {});
            skArc(sketch, "E24.9.2", {"start": v(98.32, 2.68) * mm, "mid": v(98.48, 2.38) * mm, "end": v(98.76, 2.19) * mm});
            skArc(sketch, "E24.9.3", {"start": v(98.76, 0.76) * mm, "mid": v(98.5, 0.6) * mm, "end": v(98.32, 0.33) * mm});
            skPoint(sketch, "E24.9.4", {"position": v(99.52, 1.49) * mm});
            skEllipticalArc(sketch, "E24.10.0", {});
            skEllipticalArc(sketch, "E24.10.1", {});
            skArc(sketch, "E24.10.2", {"start": v(98.3, -2.89) * mm, "mid": v(98.4, -3.21) * mm, "end": v(98.65, -3.45) * mm});
            skArc(sketch, "E24.10.3", {"start": v(98.4, -4.86) * mm, "mid": v(98.1, -4.97) * mm, "end": v(97.9, -5.2) * mm});
            skPoint(sketch, "E24.10.4", {"position": v(99.27, -4.27) * mm});
            skEllipticalArc(sketch, "E24.11.0", {});
            skEllipticalArc(sketch, "E24.11.1", {});
            skArc(sketch, "E24.11.2", {"start": v(97.31, -8.37) * mm, "mid": v(97.36, -8.7) * mm, "end": v(97.56, -8.99) * mm});
            skArc(sketch, "E24.11.3", {"start": v(97.07, -10.32) * mm, "mid": v(96.76, -10.39) * mm, "end": v(96.51, -10.57) * mm});
            skPoint(sketch, "E24.11.4", {"position": v(98.03, -9.9) * mm});
            skEllipticalArc(sketch, "E24.12.0", {});
            skEllipticalArc(sketch, "E24.12.1", {});
            skArc(sketch, "E24.12.2", {"start": v(95.4, -13.6) * mm, "mid": v(95.38, -13.93) * mm, "end": v(95.53, -14.24) * mm});
            skArc(sketch, "E24.12.3", {"start": v(94.82, -15.48) * mm, "mid": v(94.5, -15.49) * mm, "end": v(94.22, -15.63) * mm});
            skPoint(sketch, "E24.12.4", {"position": v(95.83, -15.23) * mm});
            skEllipticalArc(sketch, "E24.13.0", {});
            skEllipticalArc(sketch, "E24.13.1", {});
            skArc(sketch, "E24.13.2", {"start": v(92.6, -18.4) * mm, "mid": v(92.53, -18.74) * mm, "end": v(92.61, -19.07) * mm});
            skArc(sketch, "E24.13.3", {"start": v(91.7, -20.16) * mm, "mid": v(91.39, -20.12) * mm, "end": v(91.08, -20.2) * mm});
            skPoint(sketch, "E24.13.4", {"position": v(92.74, -20.1) * mm});
            skEllipticalArc(sketch, "E24.14.0", {});
            skEllipticalArc(sketch, "E24.14.1", {});
            skArc(sketch, "E24.14.2", {"start": v(89, -22.66) * mm, "mid": v(88.88, -22.98) * mm, "end": v(88.9, -23.32) * mm});
            skArc(sketch, "E24.14.3", {"start": v(87.81, -24.24) * mm, "mid": v(87.51, -24.14) * mm, "end": v(87.2, -24.17) * mm});
            skPoint(sketch, "E24.14.4", {"position": v(88.86, -24.35) * mm});
            skEllipticalArc(sketch, "E24.15.0", {});
            skEllipticalArc(sketch, "E24.15.1", {});
            skArc(sketch, "E24.15.2", {"start": v(84.72, -26.22) * mm, "mid": v(84.55, -26.52) * mm, "end": v(84.52, -26.86) * mm});
            skArc(sketch, "E24.15.3", {"start": v(83.28, -27.57) * mm, "mid": v(83, -27.42) * mm, "end": v(82.69, -27.4) * mm});
            skPoint(sketch, "E24.15.4", {"position": v(84.29, -27.86) * mm});
            skEllipticalArc(sketch, "E24.16.0", {});
            skEllipticalArc(sketch, "E24.16.1", {});
            skArc(sketch, "E24.16.2", {"start": v(79.9, -29) * mm, "mid": v(79.67, -29.25) * mm, "end": v(79.58, -29.58) * mm});
            skArc(sketch, "E24.16.3", {"start": v(78.24, -30.07) * mm, "mid": v(78, -29.87) * mm, "end": v(77.69, -29.8) * mm});
            skPoint(sketch, "E24.16.4", {"position": v(79.18, -30.53) * mm});
            skEllipticalArc(sketch, "E24.17.0", {});
            skEllipticalArc(sketch, "E24.17.1", {});
            skArc(sketch, "E24.17.2", {"start": v(74.65, -30.88) * mm, "mid": v(74.39, -31.1) * mm, "end": v(74.24, -31.4) * mm});
            skArc(sketch, "E24.17.3", {"start": v(72.84, -31.65) * mm, "mid": v(72.63, -31.42) * mm, "end": v(72.34, -31.29) * mm});
            skPoint(sketch, "E24.17.4", {"position": v(73.69, -32.27) * mm});
            skEllipticalArc(sketch, "E24.18.0", {});
            skEllipticalArc(sketch, "E24.18.1", {});
            skArc(sketch, "E24.18.2", {"start": v(69.17, -31.83) * mm, "mid": v(68.87, -32) * mm, "end": v(68.67, -32.27) * mm});
            skArc(sketch, "E24.18.3", {"start": v(67.25, -32.27) * mm, "mid": v(67.08, -32) * mm, "end": v(66.82, -31.83) * mm});
            skPoint(sketch, "E24.18.4", {"position": v(67.97, -33.03) * mm});
            skLineSegment(sketch, "E24.anchor1", {"start": v(66.49, 0) * mm, "end": v(63.8, 31.83) * mm, "construction": true});
            skArc(sketch, "E25.1.0", {"start": v(-85.23, -32.03) * mm, "mid": v(-85.55, -32.14) * mm, "end": v(-85.8, -32.38) * mm});
            skEllipticalArc(sketch, "E25.1.1", {});
            skArc(sketch, "E25.1.2", {"start": v(-87.2, -32.13) * mm, "mid": v(-87.31, -31.84) * mm, "end": v(-87.54, -31.62) * mm});
            skEllipticalArc(sketch, "E25.1.4", {});
            skArc(sketch, "E25.2.0", {"start": v(-90.83, -31.23) * mm, "mid": v(-91.17, -31.28) * mm, "end": v(-91.45, -31.47) * mm});
            skEllipticalArc(sketch, "E25.2.1", {});
            skArc(sketch, "E25.2.2", {"start": v(-92.79, -30.98) * mm, "mid": v(-92.85, -30.67) * mm, "end": v(-93.04, -30.42) * mm});
            skPoint(sketch, "E25.2.3", {"position": v(-92.37, -31.94) * mm});
            skEllipticalArc(sketch, "E25.2.4", {});
            skArc(sketch, "E25.3.0", {"start": v(-96.2, -29.46) * mm, "mid": v(-96.55, -29.45) * mm, "end": v(-96.86, -29.59) * mm});
            skEllipticalArc(sketch, "E25.3.1", {});
            skArc(sketch, "E25.3.2", {"start": v(-98.1, -28.87) * mm, "mid": v(-98.1, -28.55) * mm, "end": v(-98.23, -28.27) * mm});
            skPoint(sketch, "E25.3.3", {"position": v(-97.85, -29.89) * mm});
            skEllipticalArc(sketch, "E25.3.4", {});
            skArc(sketch, "E25.4.0", {"start": v(-101.19, -26.77) * mm, "mid": v(-101.52, -26.7) * mm, "end": v(-101.86, -26.78) * mm});
            skEllipticalArc(sketch, "E25.4.1", {});
            skArc(sketch, "E25.4.2", {"start": v(-102.94, -25.86) * mm, "mid": v(-102.9, -25.54) * mm, "end": v(-102.98, -25.24) * mm});
            skPoint(sketch, "E25.4.3", {"position": v(-102.88, -26.9) * mm});
            skEllipticalArc(sketch, "E25.4.4", {});
            skArc(sketch, "E25.5.0", {"start": v(-105.62, -23.24) * mm, "mid": v(-105.94, -23.11) * mm, "end": v(-106.28, -23.14) * mm});
            skEllipticalArc(sketch, "E25.5.1", {});
            skArc(sketch, "E25.5.2", {"start": v(-107.18, -22.04) * mm, "mid": v(-107.08, -21.74) * mm, "end": v(-107.1, -21.43) * mm});
            skPoint(sketch, "E25.5.3", {"position": v(-107.3, -23.08) * mm});
            skEllipticalArc(sketch, "E25.5.4", {});
            skArc(sketch, "E25.6.0", {"start": v(-109.36, -19) * mm, "mid": v(-109.65, -18.81) * mm, "end": v(-110, -18.78) * mm});
            skEllipticalArc(sketch, "E25.6.1", {});
            skArc(sketch, "E25.6.2", {"start": v(-110.69, -17.53) * mm, "mid": v(-110.54, -17.26) * mm, "end": v(-110.5, -16.94) * mm});
            skPoint(sketch, "E25.6.3", {"position": v(-111, -18.54) * mm});
            skEllipticalArc(sketch, "E25.6.4", {});
            skArc(sketch, "E25.7.0", {"start": v(-112.3, -14.15) * mm, "mid": v(-112.55, -13.92) * mm, "end": v(-112.88, -13.83) * mm});
            skEllipticalArc(sketch, "E25.7.1", {});
            skArc(sketch, "E25.7.2", {"start": v(-113.35, -12.48) * mm, "mid": v(-113.15, -12.24) * mm, "end": v(-113.07, -11.93) * mm});
            skPoint(sketch, "E25.7.3", {"position": v(-113.82, -13.42) * mm});
            skEllipticalArc(sketch, "E25.7.4", {});
            skArc(sketch, "E25.8.0", {"start": v(-114.34, -8.87) * mm, "mid": v(-114.55, -8.6) * mm, "end": v(-114.85, -8.45) * mm});
            skEllipticalArc(sketch, "E25.8.1", {});
            skArc(sketch, "E25.8.2", {"start": v(-115.08, -7.04) * mm, "mid": v(-114.84, -6.84) * mm, "end": v(-114.7, -6.55) * mm});
            skPoint(sketch, "E25.8.3", {"position": v(-115.71, -7.88) * mm});
            skEllipticalArc(sketch, "E25.8.4", {});
            skArc(sketch, "E25.9.0", {"start": v(-115.42, -3.32) * mm, "mid": v(-115.58, -3.01) * mm, "end": v(-115.85, -2.81) * mm});
            skEllipticalArc(sketch, "E25.9.1", {});
            skArc(sketch, "E25.9.2", {"start": v(-115.82, -1.38) * mm, "mid": v(-115.55, -1.22) * mm, "end": v(-115.37, -0.97) * mm});
            skPoint(sketch, "E25.9.3", {"position": v(-116.6, -2.1) * mm});
            skEllipticalArc(sketch, "E25.9.4", {});
            skArc(sketch, "E25.10.0", {"start": v(-115.5, 2.35) * mm, "mid": v(-115.6, 2.67) * mm, "end": v(-115.84, 2.92) * mm});
            skEllipticalArc(sketch, "E25.10.1", {});
            skArc(sketch, "E25.10.2", {"start": v(-115.56, 4.32) * mm, "mid": v(-115.27, 4.43) * mm, "end": v(-115.05, 4.65) * mm});
            skPoint(sketch, "E25.10.3", {"position": v(-116.45, 3.75) * mm});
            skEllipticalArc(sketch, "E25.10.4", {});
            skArc(sketch, "E25.11.0", {"start": v(-114.6, 7.93) * mm, "mid": v(-114.64, 8.27) * mm, "end": v(-114.83, 8.56) * mm});
            skEllipticalArc(sketch, "E25.11.1", {});
            skArc(sketch, "E25.11.2", {"start": v(-114.3, 9.88) * mm, "mid": v(-114, 9.94) * mm, "end": v(-113.74, 10.12) * mm});
            skPoint(sketch, "E25.11.3", {"position": v(-115.28, 9.48) * mm});
            skEllipticalArc(sketch, "E25.11.4", {});
            skArc(sketch, "E25.12.0", {"start": v(-112.71, 13.27) * mm, "mid": v(-112.7, 13.62) * mm, "end": v(-112.83, 13.93) * mm});
            skEllipticalArc(sketch, "E25.12.1", {});
            skArc(sketch, "E25.12.2", {"start": v(-112.09, 15.14) * mm, "mid": v(-111.77, 15.15) * mm, "end": v(-111.49, 15.28) * mm});
            skPoint(sketch, "E25.12.3", {"position": v(-113.11, 14.92) * mm});
            skEllipticalArc(sketch, "E25.12.4", {});
            skArc(sketch, "E25.13.0", {"start": v(-109.93, 18.2) * mm, "mid": v(-109.85, 18.53) * mm, "end": v(-109.93, 18.87) * mm});
            skEllipticalArc(sketch, "E25.13.1", {});
            skArc(sketch, "E25.13.2", {"start": v(-108.98, 19.93) * mm, "mid": v(-108.67, 19.88) * mm, "end": v(-108.37, 19.96) * mm});
            skPoint(sketch, "E25.13.3", {"position": v(-110.03, 19.9) * mm});
            skEllipticalArc(sketch, "E25.13.4", {});
            skArc(sketch, "E25.14.0", {"start": v(-106.31, 22.56) * mm, "mid": v(-106.18, 22.87) * mm, "end": v(-106.2, 23.22) * mm});
            skEllipticalArc(sketch, "E25.14.1", {});
            skArc(sketch, "E25.14.2", {"start": v(-105.08, 24.1) * mm, "mid": v(-104.78, 24) * mm, "end": v(-104.47, 24.01) * mm});
            skPoint(sketch, "E25.14.3", {"position": v(-106.12, 24.24) * mm});
            skEllipticalArc(sketch, "E25.14.4", {});
            skArc(sketch, "E25.15.0", {"start": v(-102, 26.22) * mm, "mid": v(-101.8, 26.5) * mm, "end": v(-101.76, 26.84) * mm});
            skEllipticalArc(sketch, "E25.15.1", {});
            skArc(sketch, "E25.15.2", {"start": v(-100.5, 27.51) * mm, "mid": v(-100.24, 27.36) * mm, "end": v(-99.92, 27.32) * mm});
            skPoint(sketch, "E25.15.3", {"position": v(-101.5, 27.84) * mm});
            skEllipticalArc(sketch, "E25.15.4", {});
            skArc(sketch, "E25.16.0", {"start": v(-97.1, 29.06) * mm, "mid": v(-96.86, 29.3) * mm, "end": v(-96.76, 29.63) * mm});
            skEllipticalArc(sketch, "E25.16.1", {});
            skArc(sketch, "E25.16.2", {"start": v(-95.4, 30.07) * mm, "mid": v(-95.17, 29.87) * mm, "end": v(-94.86, 29.78) * mm});
            skPoint(sketch, "E25.16.3", {"position": v(-96.33, 30.57) * mm});
            skEllipticalArc(sketch, "E25.16.4", {});
            skArc(sketch, "E25.17.0", {"start": v(-91.78, 31) * mm, "mid": v(-91.5, 31.2) * mm, "end": v(-91.35, 31.5) * mm});
            skEllipticalArc(sketch, "E25.17.1", {});
            skArc(sketch, "E25.17.2", {"start": v(-89.93, 31.7) * mm, "mid": v(-89.73, 31.45) * mm, "end": v(-89.45, 31.31) * mm});
            skPoint(sketch, "E25.17.3", {"position": v(-90.76, 32.35) * mm});
            skEllipticalArc(sketch, "E25.17.4", {});
            skArc(sketch, "E25.18.0", {"start": v(-86.2, 31.96) * mm, "mid": v(-85.9, 32.12) * mm, "end": v(-85.69, 32.39) * mm});
            skEllipticalArc(sketch, "E25.18.1", {});
            skArc(sketch, "E25.18.2", {"start": v(-84.26, 32.33) * mm, "mid": v(-84.1, 32.06) * mm, "end": v(-83.85, 31.87) * mm});
            skPoint(sketch, "E25.18.3", {"position": v(-84.96, 33.12) * mm});
            skEllipticalArc(sketch, "E25.18.4", {});
            skLineSegment(sketch, "E25.anchor2", {"start": v(-83.51, 0) * mm, "end": v(-83.54, 32.55) * mm, "construction": true});
            skLineSegment(sketch, "E26", {"start": v(69.17, -31.83) * mm, "end": v(72.34, -31.29) * mm});
            skLineSegment(sketch, "E27", {"start": v(74.65, -30.88) * mm, "end": v(77.69, -29.8) * mm});
            skLineSegment(sketch, "E28", {"start": v(79.9, -29) * mm, "end": v(82.69, -27.4) * mm});
            skLineSegment(sketch, "E29", {"start": v(84.72, -26.22) * mm, "end": v(87.2, -24.17) * mm});
            skLineSegment(sketch, "E30", {"start": v(89, -22.66) * mm, "end": v(91.08, -20.2) * mm});
            skLineSegment(sketch, "E31", {"start": v(92.6, -18.4) * mm, "end": v(94.22, -15.63) * mm});
            skLineSegment(sketch, "E32", {"start": v(95.4, -13.6) * mm, "end": v(96.51, -10.57) * mm});
            skLineSegment(sketch, "E33", {"start": v(97.31, -8.37) * mm, "end": v(97.9, -5.2) * mm});
            skPoint(sketch, "E34", {"position": v(96.51, -10.57) * mm});
            skLineSegment(sketch, "E35", {"start": v(98.3, -2.89) * mm, "end": v(98.32, 0.33) * mm});
            skLineSegment(sketch, "E36", {"start": v(98.32, 2.68) * mm, "end": v(97.77, 5.85) * mm});
            skLineSegment(sketch, "E37", {"start": v(97.37, 8.17) * mm, "end": v(96.87, 9.54) * mm});
            skArc(sketch, "E38.trimOffspring", {"start": v(96.87, 9.54) * mm, "mid": v(96.6, 10.4) * mm, "end": v(96.29, 11.25) * mm});
            skLineSegment(sketch, "E39", {"start": v(95.48, 13.4) * mm, "end": v(93.89, 16.2) * mm});
            skLineSegment(sketch, "E40", {"start": v(92.71, 18.24) * mm, "end": v(91.78, 19.36) * mm});
            skArc(sketch, "E41.trimOffspring", {"start": v(91.78, 19.36) * mm, "mid": v(91.22, 20.07) * mm, "end": v(90.64, 20.76) * mm});
            skLineSegment(sketch, "E42", {"start": v(89.15, 22.51) * mm, "end": v(88.03, 23.46) * mm});
            skArc(sketch, "E43.trimOffspring", {"start": v(88.03, 23.46) * mm, "mid": v(87.36, 24.06) * mm, "end": v(86.67, 24.64) * mm});
            skLineSegment(sketch, "E44", {"start": v(84.9, 26.1) * mm, "end": v(83.63, 26.85) * mm});
            skArc(sketch, "E45.trimOffspring", {"start": v(83.63, 26.85) * mm, "mid": v(82.86, 27.32) * mm, "end": v(82.08, 27.77) * mm});
            skLineSegment(sketch, "E46", {"start": v(80.08, 28.9) * mm, "end": v(78.8, 29.38) * mm});
            skArc(sketch, "E47.trimOffspring", {"start": v(78.8, 29.38) * mm, "mid": v(77.9, 29.74) * mm, "end": v(77, 30.07) * mm});
            skLineSegment(sketch, "E48", {"start": v(74.82, 30.76) * mm, "end": v(74.55, 30.81) * mm});
            skArc(sketch, "E49.trimOffspring", {"start": v(74.55, 30.81) * mm, "mid": v(74.52, 30.82) * mm, "end": v(74.5, 30.83) * mm});
            skLineSegment(sketch, "E50", {"start": v(74.82, 30.76) * mm, "end": v(71.62, 31.44) * mm});
            skLineSegment(sketch, "E51", {"start": v(66.49, 31.83) * mm, "end": v(69.35, 31.7) * mm});
            skLineSegment(sketch, "E52", {"start": v(65.52, -31.83) * mm, "end": v(65.61, -31.83) * mm});
            skLineSegment(sketch, "E53", {"start": v(-87.54, -31.62) * mm, "end": v(-90.83, -31.23) * mm});
            skLineSegment(sketch, "E54", {"start": v(-93.04, -30.42) * mm, "end": v(-96.2, -29.46) * mm});
            skLineSegment(sketch, "E55", {"start": v(-98.23, -28.27) * mm, "end": v(-101.19, -26.77) * mm});
            skLineSegment(sketch, "E56", {"start": v(-102.98, -25.24) * mm, "end": v(-105.62, -23.24) * mm});
            skLineSegment(sketch, "E57", {"start": v(-107.1, -21.43) * mm, "end": v(-109.36, -19) * mm});
            skLineSegment(sketch, "E58", {"start": v(-110.5, -16.94) * mm, "end": v(-112.3, -14.15) * mm});
            skLineSegment(sketch, "E59", {"start": v(-113.07, -11.93) * mm, "end": v(-114.34, -8.87) * mm});
            skLineSegment(sketch, "E60", {"start": v(-114.7, -6.55) * mm, "end": v(-115.42, -3.32) * mm});
            skLineSegment(sketch, "E61", {"start": v(-115.37, -0.97) * mm, "end": v(-115.5, 2.35) * mm});
            skLineSegment(sketch, "E62", {"start": v(-115.05, 4.65) * mm, "end": v(-114.6, 7.93) * mm});
            skLineSegment(sketch, "E63", {"start": v(-113.74, 10.12) * mm, "end": v(-112.71, 13.27) * mm});
            skLineSegment(sketch, "E64", {"start": v(-111.49, 15.28) * mm, "end": v(-109.93, 18.2) * mm});
            skLineSegment(sketch, "E65", {"start": v(-108.37, 19.96) * mm, "end": v(-106.31, 22.56) * mm});
            skLineSegment(sketch, "E66", {"start": v(-104.47, 24.01) * mm, "end": v(-102, 26.22) * mm});
            skLineSegment(sketch, "E67", {"start": v(-99.92, 27.32) * mm, "end": v(-97.1, 29.06) * mm});
            skLineSegment(sketch, "E68", {"start": v(-94.86, 29.78) * mm, "end": v(-91.78, 31) * mm});
            skLineSegment(sketch, "E69", {"start": v(-89.45, 31.31) * mm, "end": v(-86.2, 31.96) * mm});
            skLineSegment(sketch, "E70", {"start": v(-83.85, 31.87) * mm, "end": v(-83.54, 31.83) * mm});
            skArc(sketch, "E71", {"start": v(-83.51, 34.53) * mm, "mid": v(-118.04, 0) * mm, "end": v(-83.51, -34.53) * mm});
            skArc(sketch, "E72.trimOffspring", {"start": v(66.49, -34.53) * mm, "mid": v(101.14, 0.12) * mm, "end": v(66.49, 34.78) * mm});
            skLineSegment(sketch, "E73.trimOffspring", {"start": v(66.15, 31.83) * mm, "end": v(66.49, 31.83) * mm});
            skLineSegment(sketch, "E74.trimOffspring", {"start": v(61.15, 31.83) * mm, "end": v(63.8, 31.83) * mm});
            skLineSegment(sketch, "E75.trimOffspring", {"start": v(56.15, 31.83) * mm, "end": v(58.8, 31.83) * mm});
            skLineSegment(sketch, "E76.trimOffspring", {"start": v(51.15, 31.83) * mm, "end": v(53.8, 31.83) * mm});
            skLineSegment(sketch, "E77.trimOffspring", {"start": v(46.15, 31.83) * mm, "end": v(48.8, 31.83) * mm});
            skLineSegment(sketch, "E78.trimOffspring", {"start": v(41.15, 31.83) * mm, "end": v(43.8, 31.83) * mm});
            skLineSegment(sketch, "E79.trimOffspring", {"start": v(36.15, 31.83) * mm, "end": v(38.8, 31.83) * mm});
            skLineSegment(sketch, "E80.trimOffspring", {"start": v(31.15, 31.83) * mm, "end": v(33.8, 31.83) * mm});
            skLineSegment(sketch, "E81.trimOffspring", {"start": v(26.15, 31.83) * mm, "end": v(28.8, 31.83) * mm});
            skLineSegment(sketch, "E82.trimOffspring", {"start": v(21.15, 31.83) * mm, "end": v(23.8, 31.83) * mm});
            skLineSegment(sketch, "E83.trimOffspring", {"start": v(16.15, 31.83) * mm, "end": v(18.8, 31.83) * mm});
            skLineSegment(sketch, "E84.trimOffspring", {"start": v(-8.85, 31.83) * mm, "end": v(-6.2, 31.83) * mm});
            skLineSegment(sketch, "E85.trimOffspring", {"start": v(11.15, 31.83) * mm, "end": v(13.8, 31.83) * mm});
            skLineSegment(sketch, "E86.trimOffspring", {"start": v(6.15, 31.83) * mm, "end": v(8.8, 31.83) * mm});
            skLineSegment(sketch, "E87.trimOffspring", {"start": v(1.15, 31.83) * mm, "end": v(3.8, 31.83) * mm});
            skLineSegment(sketch, "E88.trimOffspring", {"start": v(-3.85, 31.83) * mm, "end": v(-1.2, 31.83) * mm});
            skLineSegment(sketch, "E89.trimOffspring", {"start": v(-13.85, 31.83) * mm, "end": v(-11.2, 31.83) * mm});
            skLineSegment(sketch, "E90.trimOffspring", {"start": v(-18.85, 31.83) * mm, "end": v(-16.2, 31.83) * mm});
            skLineSegment(sketch, "E91.trimOffspring", {"start": v(-23.85, 31.83) * mm, "end": v(-21.2, 31.83) * mm});
            skLineSegment(sketch, "E92.trimOffspring", {"start": v(-28.85, 31.83) * mm, "end": v(-26.2, 31.83) * mm});
            skLineSegment(sketch, "E93.trimOffspring", {"start": v(-33.85, 31.83) * mm, "end": v(-31.2, 31.83) * mm});
            skLineSegment(sketch, "E94.trimOffspring", {"start": v(-38.85, 31.83) * mm, "end": v(-36.2, 31.83) * mm});
            skLineSegment(sketch, "E95.trimOffspring", {"start": v(-43.85, 31.83) * mm, "end": v(-41.2, 31.83) * mm});
            skLineSegment(sketch, "E96.trimOffspring", {"start": v(-48.85, 31.83) * mm, "end": v(-46.2, 31.83) * mm});
            skLineSegment(sketch, "E97.trimOffspring", {"start": v(-53.85, 31.83) * mm, "end": v(-51.2, 31.83) * mm});
            skLineSegment(sketch, "E98.trimOffspring", {"start": v(-58.85, 31.83) * mm, "end": v(-56.2, 31.83) * mm});
            skLineSegment(sketch, "E99.trimOffspring", {"start": v(-63.85, 31.83) * mm, "end": v(-61.2, 31.83) * mm});
            skLineSegment(sketch, "E100.trimOffspring", {"start": v(-68.85, 31.83) * mm, "end": v(-66.2, 31.83) * mm, "construction": true});
            skLineSegment(sketch, "E101.trimOffspring", {"start": v(-68.85, 31.83) * mm, "end": v(-66.2, 31.83) * mm});
            skPoint(sketch, "E102.orphan", {"position": v(-74.27, 32.27) * mm});
            skLineSegment(sketch, "E103.trimOffspring", {"start": v(-73.9, 31.83) * mm, "end": v(-71.2, 31.83) * mm});
            skLineSegment(sketch, "E104.trimOffspring", {"start": v(-78.95, 31.83) * mm, "end": v(-76.24, 31.83) * mm});
            skLineSegment(sketch, "E105.trimOffspring", {"start": v(-79.57, -31.83) * mm, "end": v(-76.92, -31.83) * mm});
            skLineSegment(sketch, "E106.trimOffspring", {"start": v(-74.57, -31.83) * mm, "end": v(-71.92, -31.83) * mm});
            skLineSegment(sketch, "E107.trimOffspring", {"start": v(-69.57, -31.83) * mm, "end": v(-66.92, -31.83) * mm});
            skLineSegment(sketch, "E108.trimOffspring", {"start": v(-64.57, -31.83) * mm, "end": v(-61.92, -31.83) * mm});
            skLineSegment(sketch, "E109.trimOffspring", {"start": v(-59.57, -31.83) * mm, "end": v(-56.92, -31.83) * mm});
            skLineSegment(sketch, "E110.trimOffspring", {"start": v(-54.57, -31.83) * mm, "end": v(-51.92, -31.83) * mm});
            skLineSegment(sketch, "E111.trimOffspring", {"start": v(-49.57, -31.83) * mm, "end": v(-46.92, -31.83) * mm});
            skLineSegment(sketch, "E112.trimOffspring", {"start": v(-44.57, -31.83) * mm, "end": v(-41.92, -31.83) * mm});
            skLineSegment(sketch, "E113.trimOffspring", {"start": v(-39.57, -31.83) * mm, "end": v(-36.92, -31.83) * mm});
            skLineSegment(sketch, "E114.trimOffspring", {"start": v(-34.57, -31.83) * mm, "end": v(-31.92, -31.83) * mm});
            skLineSegment(sketch, "E115.trimOffspring", {"start": v(-29.57, -31.83) * mm, "end": v(-26.92, -31.83) * mm});
            skLineSegment(sketch, "E116.trimOffspring", {"start": v(-24.57, -31.83) * mm, "end": v(-21.92, -31.83) * mm});
            skLineSegment(sketch, "E117.trimOffspring", {"start": v(-19.57, -31.83) * mm, "end": v(-16.92, -31.83) * mm});
            skLineSegment(sketch, "E118.trimOffspring", {"start": v(-14.57, -31.83) * mm, "end": v(-11.92, -31.83) * mm});
            skLineSegment(sketch, "E119.trimOffspring", {"start": v(-9.57, -31.83) * mm, "end": v(-6.92, -31.83) * mm});
            skLineSegment(sketch, "E120.trimOffspring", {"start": v(-4.57, -31.83) * mm, "end": v(-1.92, -31.83) * mm});
            skLineSegment(sketch, "E121.trimOffspring", {"start": v(0.43, -31.83) * mm, "end": v(3.08, -31.83) * mm});
            skLineSegment(sketch, "E122.trimOffspring", {"start": v(5.43, -31.83) * mm, "end": v(8.08, -31.83) * mm});
            skLineSegment(sketch, "E123.trimOffspring", {"start": v(10.43, -31.83) * mm, "end": v(13.08, -31.83) * mm});
            skLineSegment(sketch, "E124.trimOffspring", {"start": v(15.43, -31.83) * mm, "end": v(18.08, -31.83) * mm});
            skLineSegment(sketch, "E125.trimOffspring", {"start": v(20.43, -31.83) * mm, "end": v(23.08, -31.83) * mm});
            skLineSegment(sketch, "E126.trimOffspring", {"start": v(25.43, -31.83) * mm, "end": v(28.08, -31.83) * mm});
            skLineSegment(sketch, "E127.trimOffspring", {"start": v(30.43, -31.83) * mm, "end": v(33.08, -31.83) * mm});
            skLineSegment(sketch, "E128.trimOffspring", {"start": v(35.43, -31.83) * mm, "end": v(38.08, -31.83) * mm});
            skLineSegment(sketch, "E129.trimOffspring", {"start": v(40.43, -31.83) * mm, "end": v(43.08, -31.83) * mm});
            skLineSegment(sketch, "E130.trimOffspring", {"start": v(45.43, -31.83) * mm, "end": v(48.08, -31.83) * mm});
            skLineSegment(sketch, "E131.trimOffspring", {"start": v(50.43, -31.83) * mm, "end": v(53.08, -31.83) * mm});
            skLineSegment(sketch, "E132.trimOffspring", {"start": v(55.43, -31.83) * mm, "end": v(58.13, -31.83) * mm});
            skPoint(sketch, "E133.orphan", {"position": v(58.08, -31.83) * mm});
            skPoint(sketch, "E134.start.orphan", {"position": v(58.5, -32.28) * mm});
            skLineSegment(sketch, "E135.trimOffspring", {"start": v(60.48, -31.83) * mm, "end": v(63.18, -31.83) * mm});
            skLineSegment(sketch, "E136.trimOffspring", {"start": v(65.52, -31.83) * mm, "end": v(66.49, -31.83) * mm});
            skLineSegment(sketch, "E137", {"start": v(-83.51, 34.53) * mm, "end": v(66.49, 34.78) * mm});
            skLineSegment(sketch, "E138", {"start": v(-88.36, 31.53) * mm, "end": v(-87.95, 31.65) * mm});
            skLineSegment(sketch, "E139", {"start": v(-81.92, -31.83) * mm, "end": v(-82.23, -31.83) * mm});
            skPoint(sketch, "E140.endSnap0", {"position": v(-115.44, 0.69) * mm});
            skLineSegment(sketch, "E141", {"start": v(-43.42, -32.28) * mm, "end": v(-43.35, -31.67) * mm});
            skLineSegment(sketch, "E142", {"start": v(-63.24, -34.53) * mm, "end": v(-63.38, -34.65) * mm});
            skLineSegment(sketch, "E143", {"start": v(-85.23, -32.03) * mm, "end": v(-83.51, -31.83) * mm});
            skLineSegment(sketch, "E144", {"start": v(66.82, -31.83) * mm, "end": v(66.49, -31.83) * mm});
            const initialGuessF0  = {"E9.1.0.0": [-0.070001060962677, 0.03203, 0, 1, 0.001, 0.00075, 4.958959793330928, 0], "E9.2.0.0": [-0.065001060962677, 0.03203, 0, 1, 0.001, 0.00075, 4.958959793330928, 0], "E9.3.0.0": [-0.06000106096267699, 0.03203, 0, 1, 0.001, 0.00075, 4.958959793330928, 0], "E9.4.0.0": [-0.055001060962676984, 0.03203, 0, 1, 0.001, 0.00075, 4.958959793330928, 0], "E9.5.0.0": [-0.05000106096267698, 0.03203, 0, 1, 0.001, 0.00075, 4.958959793330928, 0], "E9.6.0.0": [-0.045001060962676975, 0.03203, 0, 1, 0.001, 0.00075, 4.958959793330928, 0], "E9.7.0.0": [-0.04000106096267697, 0.03203, 0, 1, 0.001, 0.00075, 4.958959793330928, 0], "E9.8.0.0": [-0.035001060962676966, 0.03203, 0, 1, 0.001, 0.00075, 4.958959793330928, 0], "E9.9.0.0": [-0.030001060962676962, 0.03203, 0, 1, 0.001, 0.00075, 4.958959793330928, 0], "E9.10.0.0": [-0.025001060962676958, 0.03203, 0, 1, 0.001, 0.00075, 4.958959793330928, 0], "E9.11.0.0": [-0.020001060962676953, 0.03203, 0, 1, 0.001, 0.00075, 4.958959793330928, 0], "E9.12.0.0": [-0.015001060962676949, 0.03203, 0, 1, 0.001, 0.00075, 4.958959793330928, 0], "E9.13.0.0": [-0.010001060962676944, 0.03203, 0, 1, 0.001, 0.00075, 4.958959793330928, 0], "E9.14.0.0": [-0.00500106096267694, 0.03203, 0, 1, 0.001, 0.00075, 4.958959793330928, 0], "E9.15.0.0": [-1.0609626769353397e-06, 0.03203, 0, 1, 0.001, 0.00075, 4.958959793330928, 0], "E9.16.0.0": [0.004998939037323069, 0.03203, 0, 1, 0.001, 0.00075, 4.958959793330928, 0], "E9.17.0.0": [0.009998939037323074, 0.03203, 0, 1, 0.001, 0.00075, 4.958959793330928, 0], "E9.18.0.0": [0.014998939037323078, 0.03203, 0, 1, 0.001, 0.00075, 4.958959793330928, 0], "E9.19.0.0": [0.019998939037323082, 0.03203, 0, 1, 0.001, 0.00075, 4.958959793330928, 0], "E9.20.0.0": [0.024998939037323087, 0.03203, 0, 1, 0.001, 0.00075, 4.958959793330928, 0], "E9.21.0.0": [0.02999893903732309, 0.03203, 0, 1, 0.001, 0.00075, 4.958959793330928, 0], "E9.22.0.0": [0.034998939037323096, 0.03203, 0, 1, 0.001, 0.00075, 4.958959793330928, 0], "E9.23.0.0": [0.0399989390373231, 0.03203, 0, 1, 0.001, 0.00075, 4.958959793330928, 0], "E9.24.0.0": [0.044998939037323105, 0.03203, 0, 1, 0.001, 0.00075, 4.958959793330928, 0], "E9.25.0.0": [0.04999893903732311, 0.03203, 0, 1, 0.001, 0.00075, 4.958959793330928, 0], "E9.26.0.0": [0.054998939037323114, 0.03203, 0, 1, 0.001, 0.00075, 4.958959793330928, 0], "E9.27.0.0": [0.05999893903732312, 0.03203, 0, 1, 0.001, 0.00075, 4.958959793330928, 0], "E9.28.0.0": [0.06499893903732312, 0.03203, 0, 1, 0.001, 0.00075, 4.958959793330928, 0], "E10": [-0.070001060962677, 0.03203, 0, 1, 0.001, 0.0007199110732306023, 0, 1.3242255138486574], "E12.1.0.0": [-0.065001060962677, 0.03203, 0, 1, 0.001, 0.0007199110732306023, 0, 1.3242255138486574], "E12.2.0.0": [-0.06000106096267699, 0.03203, 0, 1, 0.001, 0.0007199110732306023, 0, 1.3242255138486574], "E13.0.3.0": [-0.055001060962676984, 0.03203, 0, 1, 0.001, 0.0007199110732306023, 0, 1.3242255138486574], "E13.0.4.0": [-0.05000106096267698, 0.03203, 0, 1, 0.001, 0.0007199110732306023, 0, 1.3242255138486574], "E13.0.5.0": [-0.045001060962676975, 0.03203, 0, 1, 0.001, 0.0007199110732306023, 0, 1.3242255138486574], "E13.0.6.0": [-0.04000106096267697, 0.03203, 0, 1, 0.001, 0.0007199110732306023, 0, 1.3242255138486574], "E13.0.7.0": [-0.035001060962676966, 0.03203, 0, 1, 0.001, 0.0007199110732306023, 0, 1.3242255138486574], "E13.0.8.0": [-0.030001060962676962, 0.03203, 0, 1, 0.001, 0.0007199110732306023, 0, 1.3242255138486574], "E13.0.9.0": [-0.025001060962676958, 0.03203, 0, 1, 0.001, 0.0007199110732306023, 0, 1.3242255138486574], "E13.0.10.0": [-0.020001060962676953, 0.03203, 0, 1, 0.001, 0.0007199110732306023, 0, 1.3242255138486574], "E13.0.11.0": [-0.015001060962676949, 0.03203, 0, 1, 0.001, 0.0007199110732306023, 0, 1.3242255138486574], "E13.0.12.0": [-0.010001060962676944, 0.03203, 0, 1, 0.001, 0.0007199110732306023, 0, 1.3242255138486574], "E13.0.13.0": [-0.00500106096267694, 0.03203, 0, 1, 0.001, 0.0007199110732306023, 0, 1.3242255138486574], "E13.0.14.0": [-1.0609626745090037e-06, 0.03203, 0, 1, 0.001, 0.0007199110732306023, 0, 1.324225513848658], "E13.0.15.0": [0.004998939037323069, 0.03203, 0, 1, 0.001, 0.0007199110732306023, 0, 1.3242255138486574], "E13.0.16.0": [0.009998939037323074, 0.03203, 0, 1, 0.001, 0.0007199110732306023, 0, 1.3242255138486574], "E13.0.17.0": [0.014998939037323078, 0.03203, 0, 1, 0.001, 0.0007199110732306023, 0, 1.3242255138486574], "E13.0.18.0": [0.019998939037323082, 0.03203, 0, 1, 0.001, 0.0007199110732306023, 0, 1.3242255138486574], "E13.0.19.0": [0.024998939037323087, 0.03203, 0, 1, 0.001, 0.0007199110732306023, 0, 1.3242255138486574], "E13.0.20.0": [0.02999893903732309, 0.03203, 0, 1, 0.001, 0.0007199110732306023, 0, 1.3242255138486574], "E13.0.21.0": [0.034998939037323096, 0.03203, 0, 1, 0.001, 0.0007199110732306023, 0, 1.3242255138486574], "E13.0.22.0": [0.0399989390373231, 0.03203, 0, 1, 0.001, 0.0007199110732306023, 0, 1.3242255138486574], "E13.0.23.0": [0.044998939037323105, 0.03203, 0, 1, 0.001, 0.0007199110732306023, 0, 1.3242255138486574], "E13.0.24.0": [0.04999893903732311, 0.03203, 0, 1, 0.001, 0.0007199110732306023, 0, 1.3242255138486574], "E13.0.25.0": [0.054998939037323114, 0.03203, 0, 1, 0.001, 0.0007199110732306023, 0, 1.3242255138486574], "E13.0.26.0": [0.05999893903732312, 0.03203, 0, 1, 0.001, 0.0007199110732306023, 0, 1.3242255138486574], "E13.0.27.0": [0.06499893903732312, 0.03203, 0, 1, 0.001, 0.0007199110732306023, 0, 1.3242255138486574], "E14.1.0.0": [-0.07504554050207138, 0.03203, 0, 1, 0.001, 0.0007199110732306023, 0, 1.3242255138486574], "E14.2.0.0": [-0.08009002004146576, 0.03203, 0, 1, 0.001, 0.0007199110732306023, 0, 1.3242255138486574], "E15.1.0.0": [-0.075051060962677, 0.03203, 0, 1, 0.001, 0.00075, 4.958959793330928, 0], "E15.2.0.0": [-0.080101060962677, 0.03203, 0, 1, 0.001, 0.00075, 4.958959793330928, 0], "E17.1.0.0": [0.0542360627763388, -0.03203221367762847, 0, -1, 0.001, 0.00075, 4.95895979309259, 6.2831853071795845], "E17.2.0.0": [0.049236062776338796, -0.03203221367762848, 0, -1, 0.001, 0.00075, 4.95895979309259, 6.2831853071795845], "E17.3.0.0": [0.04423606277633879, -0.032032213677628485, 0, -1, 0.001, 0.00075, 4.95895979309259, 6.2831853071795845], "E17.4.0.0": [0.03923606277633879, -0.03203221367762849, 0, -1, 0.001, 0.00075, 4.95895979309259, 6.2831853071795845], "E17.5.0.0": [0.03423606277633878, -0.0320322136776285, 0, -1, 0.001, 0.00075, 4.95895979309259, 6.2831853071795845], "E17.6.0.0": [0.029236062776338778, -0.0320322136776285, 0, -1, 0.001, 0.00075, 4.95895979309259, 6.2831853071795845], "E17.7.0.0": [0.024236062776338774, -0.032032213677628506, 0, -1, 0.001, 0.00075, 4.95895979309259, 6.2831853071795845], "E17.8.0.0": [0.01923606277633877, -0.03203221367762851, 0, -1, 0.001, 0.00075, 4.95895979309259, 6.2831853071795845], "E17.9.0.0": [0.014236062776338765, -0.03203221367762852, 0, -1, 0.001, 0.00075, 4.95895979309259, 0], "E17.10.0.0": [0.00923606277633876, -0.03203221367762853, 0, -1, 0.001, 0.00075, 4.95895979309259, 0], "E17.11.0.0": [0.004236062776338756, -0.032032213677628533, 0, -1, 0.001, 0.00075, 4.95895979309259, 6.283185307179585], "E17.12.0.0": [-0.0007639372236612485, -0.03203221367762854, 0, -1, 0.001, 0.00075, 4.95895979309259, 0], "E17.13.0.0": [-0.005763937223661253, -0.03203221367762855, 0, -1, 0.001, 0.00075, 4.95895979309259, 6.283185307179585], "E17.14.0.0": [-0.010763937223661257, -0.032032213677628554, 0, -1, 0.001, 0.00075, 4.95895979309259, 0], "E17.15.0.0": [-0.015763937223661262, -0.03203221367762856, 0, -1, 0.001, 0.00075, 4.95895979309259, 6.2831853071795845], "E17.16.0.0": [-0.020763937223661266, -0.03203221367762856, 0, -1, 0.001, 0.00075, 4.95895979309259, 6.2831853071795845], "E17.17.0.0": [-0.02576393722366127, -0.03203221367762857, 0, -1, 0.001, 0.00075, 4.95895979309259, 6.2831853071795845], "E17.18.0.0": [-0.030763937223661275, -0.032032213677628575, 0, -1, 0.001, 0.00075, 4.95895979309259, 6.2831853071795845], "E17.19.0.0": [-0.03576393722366128, -0.03203221367762858, 0, -1, 0.001, 0.00075, 4.95895979309259, 6.2831853071795845], "E17.20.0.0": [-0.040763937223661284, -0.03203221367762859, 0, -1, 0.001, 0.00075, 4.95895979309259, 6.2831853071795845], "E17.21.0.0": [-0.04576393722366129, -0.032032213677628596, 0, -1, 0.001, 0.00075, 4.95895979309259, 6.2831853071795845], "E17.22.0.0": [-0.05076393722366129, -0.0320322136776286, 0, -1, 0.001, 0.00075, 4.95895979309259, 6.2831853071795845], "E17.23.0.0": [-0.0557639372236613, -0.03203221367762861, 0, -1, 0.001, 0.00075, 4.95895979309259, 6.2831853071795845], "E17.24.0.0": [-0.0607639372236613, -0.03203221367762862, 0, -1, 0.001, 0.00075, 4.95895979309259, 6.2831853071795845], "E17.25.0.0": [-0.0657639372236613, -0.032032213677628624, 0, -1, 0.001, 0.00075, 4.95895979309259, 6.2831853071795845], "E17.26.0.0": [-0.07076393722366131, -0.032032213677628624, 0, -1, 0.001, 0.00075, 4.95895979309259, 6.2831853071795845], "E17.27.0.0": [-0.07576393722366132, -0.03203221367762863, 0, -1, 0.001, 0.00075, 4.95895979309259, 6.2831853071795845], "E17.28.0.0": [-0.08076393722366144, -0.03203221367762865, 0, -1, 0.001, 0.00075, 4.958959793092605, 0], "E18": [0.0542360627763388, -0.03203221367762847, 0, -1, 0.001, 0.000719911073231896, 6.2831853071795845, 1.3242255140863497], "E20.1.0.0": [0.049236062776338796, -0.03203221367762848, 0, -1, 0.001, 0.000719911073231896, 6.2831853071795845, 1.3242255140863497], "E20.2.0.0": [0.04423606277633879, -0.032032213677628485, 0, -1, 0.001, 0.000719911073231896, 6.2831853071795845, 1.324225514086351], "E21.0.3.0": [0.03923606277633879, -0.03203221367762849, 0, -1, 0.001, 0.000719911073231896, 6.2831853071795845, 1.3242255140863524], "E21.0.4.0": [0.03423606277633878, -0.0320322136776285, 0, -1, 0.001, 0.000719911073231896, 6.2831853071795845, 1.3242255140863524], "E21.0.5.0": [0.029236062776338778, -0.032032213677628506, 0, -1, 0.001, 0.000719911073231896, 6.2831853071795845, 1.324225514086353], "E21.0.6.0": [0.024236062776338774, -0.032032213677628506, 0, -1, 0.001, 0.000719911073231896, 6.2831853071795845, 1.3242255140863537], "E21.0.7.0": [0.01923606277633877, -0.03203221367762851, 0, -1, 0.001, 0.000719911073231896, 6.2831853071795845, 1.3242255140863548], "E21.0.8.0": [0.014236062776338765, -0.03203221367762852, 0, -1, 0.001, 0.000719911073231896, 0, 1.3242255140863548], "E21.0.9.0": [0.00923606277633876, -0.03203221367762853, 0, -1, 0.001, 0.000719911073231896, 0, 1.3242255140863548], "E21.0.10.0": [0.004236062776338756, -0.032032213677628533, 0, -1, 0.001, 0.000719911073231896, 6.283185307179585, 1.3242255140863561], "E21.0.11.0": [-0.0007639372236612485, -0.03203221367762854, 0, -1, 0.001, 0.000719911073231896, 0, 1.3242255140863572], "E21.0.12.0": [-0.005763937223661253, -0.03203221367762855, 0, -1, 0.001, 0.000719911073231896, 6.283185307179585, 1.3242255140863572], "E21.0.13.0": [-0.010763937223661257, -0.032032213677628554, 0, -1, 0.001, 0.000719911073231896, 0, 1.3242255140863572], "E21.0.14.0": [-0.015763937223661262, -0.03203221367762856, 0, -1, 0.001, 0.000719911073231896, 6.2831853071795845, 1.32422551408636], "E21.0.15.0": [-0.020763937223661266, -0.03203221367762857, 0, -1, 0.001, 0.000719911073231896, 6.2831853071795845, 1.32422551408636], "E21.0.16.0": [-0.02576393722366127, -0.03203221367762857, 0, -1, 0.001, 0.000719911073231896, 6.2831853071795845, 1.32422551408636], "E21.0.17.0": [-0.030763937223661275, -0.032032213677628575, 0, -1, 0.001, 0.000719911073231896, 6.2831853071795845, 1.32422551408636], "E21.0.18.0": [-0.03576393722366128, -0.03203221367762858, 0, -1, 0.001, 0.000719911073231896, 6.2831853071795845, 1.32422551408636], "E21.0.19.0": [-0.040763937223661284, -0.03203221367762859, 0, -1, 0.001, 0.000719911073231896, 6.2831853071795845, 1.3242255140863624], "E21.0.20.0": [-0.04576393722366129, -0.032032213677628596, 0, -1, 0.001, 0.000719911073231896, 6.2831853071795845, 1.3242255140863624], "E21.0.21.0": [-0.05076393722366129, -0.0320322136776286, 0, -1, 0.001, 0.000719911073231896, 6.2831853071795845, 1.3242255140863624], "E21.0.22.0": [-0.0557639372236613, -0.03203221367762861, 0, -1, 0.001, 0.000719911073231896, 6.2831853071795845, 1.3242255140863648], "E21.0.23.0": [-0.0607639372236613, -0.03203221367762862, 0, -1, 0.001, 0.000719911073231896, 6.2831853071795845, 1.3242255140863648], "E21.0.24.0": [-0.0657639372236613, -0.032032213677628624, 0, -1, 0.001, 0.000719911073231896, 6.2831853071795845, 1.3242255140863648], "E21.0.25.0": [-0.07076393722366131, -0.03203221367762863, 0, -1, 0.001, 0.000719911073231896, 6.2831853071795845, 1.3242255140863648], "E21.0.26.0": [-0.07576393722366132, -0.03203221367762863, 0, -1, 0.001, 0.000719911073231896, 6.2831853071795845, 1.3242255140863648], "E21.0.27.0": [-0.08076393722366133, -0.032032213677628645, 0, -1, 0.001, 0.000719911073231896, 6.2831853071795845, 1.3242255140880823], "E22.1.0.0": [0.05928054231573318, -0.032032213677628464, 0, -1, 0.001, 0.000719911073231896, 6.2831853071795845, 1.3242255140863497], "E22.2.0.0": [0.06432502185512756, -0.03203221367762846, 0, -1, 0.001, 0.000719911073231896, 6.2831853071795845, 1.3242255140863497], "E23.1.0.0": [0.0592860627763388, -0.032032213677628464, 0, -1, 0.001, 0.00075, 4.95895979309259, 6.2831853071795845], "E23.2.0.0": [0.0643360627763388, -0.03203221367762846, 0, -1, 0.001, 0.00075, 4.95895979309259, 6.2831853071795845], "E24.1.0": [0.0705638248067358, 0.03174136017981966, 0.1282244304804869, 0.9917451766597885, 0.001, 0.00075, 4.958959793330926, 0], "E24.1.1": [0.0705638248067358, 0.03174136017981966, 0.1282244304804869, 0.9917451766597885, 0.001, 0.0007199110732306024, 0, 1.3242255138486587], "E24.2.0": [0.07601473682218404, 0.030572864604736034, 0.3156490369471024, 0.9488760116444966, 0.001, 0.00075, 4.958959793330928, 0], "E24.2.1": [0.07601473682218404, 0.030572864604736034, 0.3156490369471024, 0.9488760116444966, 0.001, 0.0007199110732306024, 0, 1.3242255138486607], "E24.3.0": [0.08121315224884718, 0.028482267510162317, 0.5, 0.8660254037844387, 0.001, 0.00075, 4.958959793330928, 0], "E24.3.1": [0.08121315224884718, 0.028482267510162317, 0.5, 0.8660254037844387, 0.001, 0.0007199110732306023, 0, 1.3242255138486574], "E24.4.0": [0.08593530584200255, 0.02549219504127607, 0.6427876096865394, 0.7660444431189782, 0.001, 0.00075, 4.958959793330928, 0], "E24.4.1": [0.08593530584200255, 0.02549219504127607, 0.6427876096865394, 0.7660444431189782, 0.001, 0.0007199110732306023, 0, 1.3242255138486574], "E24.5.0": [0.09006649867614228, 0.021727555125733766, 0.766044443118978, 0.6427876096865394, 0.001, 0.00075, 4.958959793330928, 0], "E24.5.1": [0.09006649867614228, 0.021727555125733766, 0.766044443118978, 0.6427876096865394, 0.001, 0.0007199110732306023, 0, 1.3242255138486574], "E24.6.0": [0.09348120654748543, 0.01730273444236944, 0.8660254037844386, 0.5, 0.001, 0.00075, 4.958959793330928, 0], "E24.6.1": [0.09348120654748543, 0.01730273444236944, 0.8660254037844386, 0.5, 0.001, 0.0007199110732306023, 0, 1.3242255138486574], "E24.7.0": [0.09607567528528684, 0.012352178928579802, 0.9396926207859085, 0.3420201433256689, 0.001, 0.00075, 4.958959793330928, 0], "E24.7.1": [0.09607567528528684, 0.012352178928579802, 0.9396926207859085, 0.3420201433256689, 0.001, 0.0007199110732306023, 0, 1.3242255138486574], "E24.8.0": [0.09777107326981345, 0.007026308708546794, 0.984807753012208, 0.17364817766693041, 0.001, 0.00075, 4.958959793330921, 0], "E24.8.1": [0.09777107326981291, 0.007026308708549402, 0.9848077530122082, 0.17364817766693044, 0.001, 0.0007199110732306023, 0, 1.3242255138486574], "E24.9.0": [0.09851588669121661, 0.0014869476538934834, 1, 0, 0.001, 0.00075, 4.958959793330928, 0], "E24.9.1": [0.09851588669121686, 0.0014869476538908327, 1, 0, 0.001, 0.0007199110732306023, 0, 1.324225513848658], "E24.10.0": [0.09828748477058236, -0.004097593552794154, 0.9848077530122082, -0.17364817766693033, 0.001, 0.00075, 4.958959793330928, 0], "E24.10.1": [0.09828748477058236, -0.004097593552794154, 0.9848077530122082, -0.17364817766693033, 0.001, 0.0007199110732306023, 0, 1.3242255138486574], "E24.11.0": [0.09709280738469167, -0.009557631452862536, 0.9396926207859086, -0.34202014332566855, 0.001, 0.00075, 4.958959793330928, 0], "E24.11.1": [0.09709280738469167, -0.009557631452862536, 0.9396926207859086, -0.34202014332566855, 0.001, 0.0007199110732306023, 0, 1.3242255138486574], "E24.12.0": [0.09496815420137893, -0.01472726555763057, 0.8660254037844389, -0.5, 0.001, 0.00075, 4.958959793330928, 0], "E24.12.1": [0.09496815420137893, -0.01472726555763057, 0.8660254037844389, -0.5, 0.001, 0.0007199110732306023, 0, 1.3242255138486574], "E24.13.0": [0.09197808173248975, -0.019449419150788117, 0.766044443118978, -0.6427876096865394, 0.001, 0.00075, 4.958959793330933, 0], "E24.13.1": [0.09197808173249268, -0.01944941915078595, 0.766044443118978, -0.6427876096865394, 0.001, 0.0007199110732306023, 0, 1.3242255138486574], "E24.14.0": [0.08821344181695037, -0.023580611984925663, 0.6427876096865395, -0.7660444431189779, 0.001, 0.00075, 4.958959793330928, 0], "E24.14.1": [0.08821344181694847, -0.023580611984927512, 0.6427876096865395, -0.7660444431189779, 0.001, 0.0007199110732306023, 0, 1.3242255138486574], "E24.15.0": [0.08378862113358605, -0.02699531985626883, 0.5, -0.8660254037844385, 0.001, 0.00075, 4.958959793330928, 0], "E24.15.1": [0.08378862113358605, -0.02699531985626883, 0.5, -0.8660254037844385, 0.001, 0.0007199110732306023, 0, 1.3242255138486574], "E24.16.0": [0.0788380656197964, -0.02958978859407023, 0.34202014332566893, -0.9396926207859085, 0.001, 0.00075, 4.958959793330928, 0], "E24.16.1": [0.0788380656197964, -0.02958978859407023, 0.34202014332566893, -0.9396926207859085, 0.001, 0.0007199110732306023, 0, 1.3242255138486574], "E24.17.0": [0.07351219539976601, -0.03128518657859631, 0.1736481776669303, -0.9848077530122082, 0.001, 0.00075, 4.958959793330928, 0], "E24.17.1": [0.07351219539976601, -0.03128518657859631, 0.1736481776669303, -0.9848077530122082, 0.001, 0.0007199110732306023, 0, 1.3242255138486574], "E24.18.0": [0.06797283434511009, -0.03203, 0, -1, 0.001, 0.00075, 4.958959793330928, 0], "E24.18.1": [0.06797283434511009, -0.03203, 0, -1, 0.001, 0.0007199110732306023, 0, 1.3242255138486574], "E25.1.1": [-0.08643832728178807, -0.032016794877509545, -0.17580908229077555, -0.984424281793209, 0.001, 0.00075, 4.958959793092595, 6.2831853071795845], "E25.1.4": [-0.08643832728178796, -0.032016794877509545, -0.1758090822907682, -0.9844242817932103, 0.001, 0.000719911073231896, 0, 1.324225514086359], "E25.2.1": [-0.09202162387427494, -0.031004006927597062, -0.34614145913363376, -0.9381823331681529, 0.001, 0.00075, 4.958959793092597, 6.283185307179581], "E25.2.4": [-0.09202162387427484, -0.031004006927597083, -0.3461414591336269, -0.9381823331681555, 0.001, 0.000719911073231896, 0, 1.3242255140863484], "E25.3.1": [-0.09733989929234305, -0.02902539962731336, -0.5056910323221867, -0.8627146572470652, 0.001, 0.00075, 4.958959793092602, 0], "E25.3.4": [-0.09733989929234296, -0.029025399627313396, -0.5056910323221807, -0.8627146572470688, 0.001, 0.000719911073231896, 0, 1.3242255140863401], "E25.4.1": [-0.10222748161747654, -0.026142609436160667, -0.6494876034724376, -0.7603721805376823, 0.001, 0.00075, 4.95895979309259, 0], "E25.4.4": [-0.10222748161747644, -0.02614260943616073, -0.6494876034724317, -0.7603721805376873, 0.001, 0.000719911073231896, 6.283185307179582, 1.3242255140863366], "E25.5.1": [-0.10653211563965787, -0.022445439409472356, -0.7730517028417087, -0.6343430181956247, 0.001, 0.00075, 4.958959793092597, 0], "E25.5.4": [-0.1065321156396578, -0.022445439409472433, -0.7730517028417038, -0.6343430181956307, 0.001, 0.000719911073231896, 6.2831853071795845, 1.324225514086339], "E25.6.1": [-0.11011970582586134, -0.018049061704245, -0.8725341312454966, -0.4885531596578479, 0.001, 0.00075, 4.958959793092616, 0], "E25.6.4": [-0.11011970582586125, -0.018049061704245098, -0.8725341312454928, -0.48855315965785473, 0.001, 0.000719911073231896, 6.283185307179585, 1.3242255140863197], "E25.7.1": [-0.11287849358852342, -0.01309042980101309, -0.9448358681411124, -0.32754416843233614, 0.001, 0.00075, 4.958959793092623, 6.283185307179584], "E25.7.4": [-0.11287849358852338, -0.0130904298010132, -0.9448358681411099, -0.32754416843234346, 0.001, 0.000719911073231896, 0, 1.3242255140862993], "E25.8.1": [-0.11472253872607702, -0.007724012206208511, -0.9877046105690609, -0.15633170587126563, 0.001, 0.00075, 4.9589597930926015, 0], "E25.8.4": [-0.114722538726077, -0.007724012206208622, -0.9877046105690597, -0.15633170587127332, 0.001, 0.000719911073231896, 0, 1.324225514086307], "E25.9.1": [-0.11559439658367587, -0.002116980536304394, -0.9998049356254678, 0.01975071388468033, 0.001, 0.00075, 4.958959793092591, 0], "E25.9.4": [-0.11559439658367587, -0.0021169805363043526, -0.9998049356254678, 0.01975071388468033, 0.001, 0.000719911073231896, 0, 1.3242255140863746], "E25.10.1": [-0.11546690753670724, 0.0035559981181649963, -0.9807599008037545, 0.1952178705329244, 0.001, 0.00075, 4.958959793092604, 0], "E25.10.4": [-0.11546690753670726, 0.0035559981181648853, -0.9807599008037562, 0.1952178705329168, 0.001, 0.000719911073231896, 0, 1.3242255140862804], "E25.11.1": [-0.11434404305211128, 0.009118202323369684, -0.9311627862951645, 0.36460371010046777, 0.001, 0.00075, 4.958959793092588, 6.283185307179583], "E25.11.4": [-0.11434404305211131, 0.00911820232336956, -0.9311627862951672, 0.3646037101004606, 0.001, 0.000719911073231896, 0, 1.3242255140862764], "E25.12.1": [-0.11226078197148091, 0.014396361428691731, -0.8525586134586087, 0.5226316203766612, 0.001, 0.00075, 4.958959793092567, 0], "E25.12.4": [-0.11226078197148096, 0.014396361428691634, -0.8525586134586128, 0.5226316203766546, 0.001, 0.000719911073231896, 6.283185307179582, 1.3242255140862773], "E25.13.1": [-0.10928202086990223, 0.019226053196380988, -0.7473960151860475, 0.664378804962965, 0.001, 0.00075, 4.958959793092608, 0], "E25.13.4": [-0.1092820208699023, 0.019226053196380904, -0.7473960151860526, 0.6643788049629592, 0.001, 0.000719911073231896, 0, 1.324225514086264], "E25.14.1": [-0.1055005524344224, 0.02345682579043907, -0.6189509574706552, 0.7854296354519348, 0.001, 0.00075, 4.958959793092591, 6.283185307179585], "E25.14.4": [-0.10550055243442247, 0.023456825790439007, -0.6189509574706613, 0.78542963545193, 0.001, 0.000719911073231896, 0, 1.3242255140862709], "E25.15.1": [-0.10103417483855916, 0.026956884567421888, -0.4712246883604915, 0.8820132045947826, 0.001, 0.00075, 4.9589597930926, 6.283185307179578], "E25.15.4": [-0.10103417483855924, 0.026956884567421825, -0.4712246883604983, 0.8820132045947789, 0.001, 0.000719911073231896, 0, 1.3242255140862493], "E25.16.1": [-0.09602202215998909, 0.029617197668894445, -0.3088190933343569, 0.9511207954787582, 0.001, 0.00075, 4.958959793092603, 0], "E25.16.4": [-0.0960220221599892, 0.02961719766889441, -0.30881909333436425, 0.9511207954787558, 0.001, 0.000719911073231896, 0, 1.3242255140862411], "E25.17.1": [-0.09062023015417389, 0.03135489252043602, -0.13679333995891782, 0.9905996073807439, 0.001, 0.00075, 4.958959793092568, 6.283185307179583], "E25.17.4": [-0.090620230154174, 0.031354892520435995, -0.13679333995892554, 0.9905996073807428, 0.001, 0.000719911073231896, 0, 1.32422551408623], "E25.18.1": [-0.08499707240130201, 0.0321158374313726, 0.0394937224480527, 0.9992198186020913, 0.001, 0.00075, 4.958959793092587, 6.283185307179581], "E25.18.4": [-0.08499707240130211, 0.03211583743137259, 0.039493722448044964, 0.9992198186020916, 0.001, 0.000719911073231896, 0, 1.3242255140862182]};
            skSetInitialGuess(sketch, initialGuessF0);
            skSolve(sketch);
        }
        {
            var Q0;
            Q0=makeQuery(id+"F0.imprint","IMPRINT",FACE,{"disambiguationData":[TD([[makeQuery(id+"F0.imprint","IMPRINT",EDGE,{"derivedFrom":sQuery(id+"F0.wireOp",EDGE,"E3")}),-1.0]])]});
            extrude(context, id + "F1", {"entities" : qUnion([Q0]), "depth" : 10 * mm, "offsetDistance" : 25 * mm});
        }
    });
